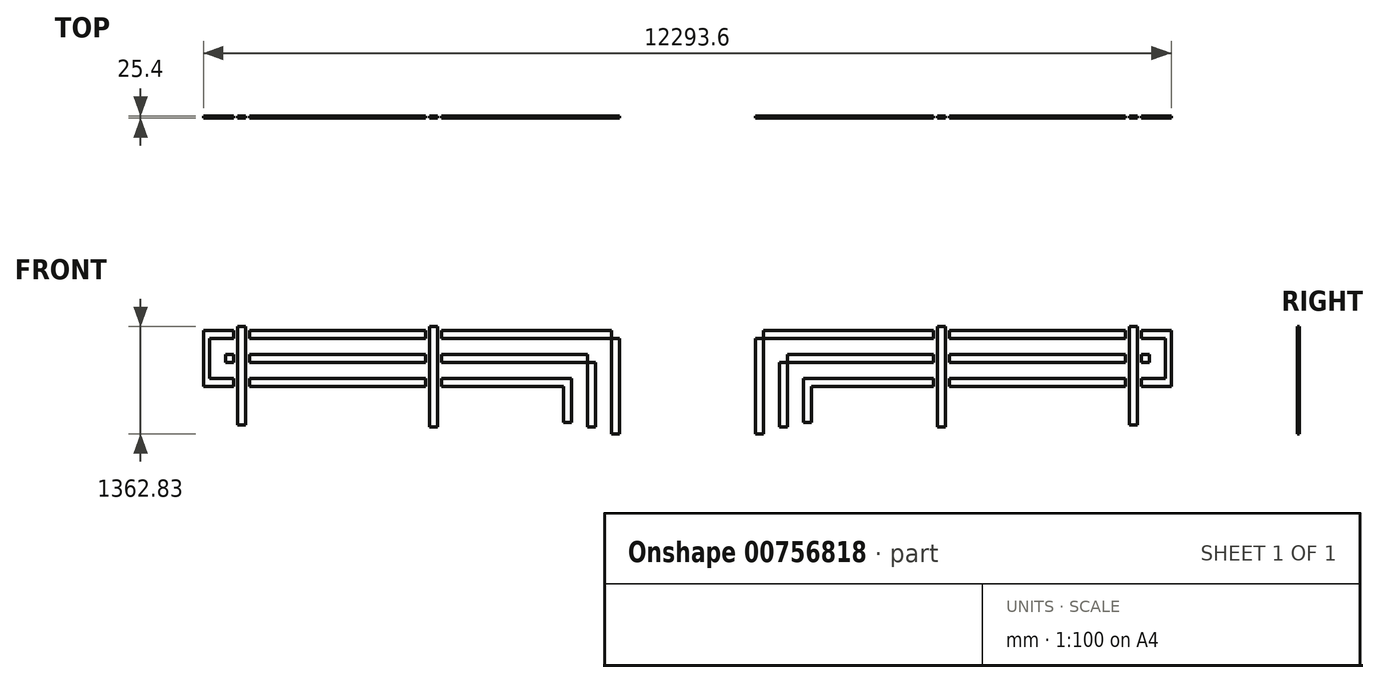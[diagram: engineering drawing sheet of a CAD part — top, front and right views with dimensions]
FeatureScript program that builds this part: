
annotation { "Feature Type Name" : "Feature", "Feature Type Description" : "" }
export const myFeature = defineFeature(function(context is Context, id is Id, definition is map)
    precondition{}
    {
        {
            var Q0;
            Q0=qCreatedBy(makeId("Front.planeOp"),FACE);
            var sketch = newSketch(context, id + "F0", { "sketchPlane" : qUnion([Q0])});
            skLineSegment(sketch, "E0.bottom", {"start": v(-6267.86, -850.3) * mm, "end": v(8083.14, -850.3) * mm});
            skLineSegment(sketch, "E0.top", {"start": v(-6267.86, 673.7) * mm, "end": v(8083.14, 673.7) * mm});
            skLineSegment(sketch, "E0.left", {"start": v(-6267.86, -850.3) * mm, "end": v(-6267.86, 673.7) * mm});
            skLineSegment(sketch, "E0.right", {"start": v(8083.14, -850.3) * mm, "end": v(8083.14, 673.7) * mm});
            skLineSegment(sketch, "E1", {"start": v(-6267.86, -88.3) * mm, "end": v(8083.14, -88.3) * mm});
            skLineSegment(sketch, "E2", {"start": v(82.14, 610.2) * mm, "end": v(56.74, 610.2) * mm});
            skLineSegment(sketch, "E3", {"start": v(82.14, 610.2) * mm, "end": v(82.14, -786.8) * mm});
            skLineSegment(sketch, "E4", {"start": v(82.14, -786.8) * mm, "end": v(56.74, -786.8) * mm});
            skLineSegment(sketch, "E5", {"start": v(56.74, 610.2) * mm, "end": v(-2229.26, 610.2) * mm});
            skLineSegment(sketch, "E6", {"start": v(-2229.26, 610.2) * mm, "end": v(-2229.26, 584.8) * mm});
            skLineSegment(sketch, "E7", {"start": v(-2229.26, 584.8) * mm, "end": v(-2229.26, 457.8) * mm});
            skLineSegment(sketch, "E8", {"start": v(-2229.26, 457.8) * mm, "end": v(-2229.26, 432.4) * mm});
            skLineSegment(sketch, "E9", {"start": v(-2229.26, 432.4) * mm, "end": v(-2229.26, 305.4) * mm});
            skLineSegment(sketch, "E10", {"start": v(-2229.26, 305.4) * mm, "end": v(-2229.26, 280) * mm});
            skLineSegment(sketch, "E11", {"start": v(-2229.26, 280) * mm, "end": v(-2229.26, 153) * mm});
            skLineSegment(sketch, "E12", {"start": v(-2229.26, 153) * mm, "end": v(-2229.26, 127.6) * mm});
            skLineSegment(sketch, "E13", {"start": v(-2229.26, 127.6) * mm, "end": v(-2229.26, 0.6) * mm});
            skLineSegment(sketch, "E14", {"start": v(-2229.26, 0.6) * mm, "end": v(-2229.26, -24.8) * mm});
            skLineSegment(sketch, "E15", {"start": v(-2229.26, -24.8) * mm, "end": v(-2229.26, -151.8) * mm});
            skLineSegment(sketch, "E16", {"start": v(-2229.26, -151.8) * mm, "end": v(-2229.26, -177.2) * mm});
            skLineSegment(sketch, "E17", {"start": v(-2229.26, 584.8) * mm, "end": v(56.74, 584.8) * mm});
            skLineSegment(sketch, "E18", {"start": v(56.74, 610.2) * mm, "end": v(-70.26, 610.2) * mm});
            skLineSegment(sketch, "E19", {"start": v(-70.26, 610.2) * mm, "end": v(-95.66, 610.2) * mm});
            skLineSegment(sketch, "E20", {"start": v(-95.66, 610.2) * mm, "end": v(-222.66, 610.2) * mm});
            skLineSegment(sketch, "E21", {"start": v(-222.66, 610.2) * mm, "end": v(-248.06, 610.2) * mm});
            skLineSegment(sketch, "E22", {"start": v(-248.06, 610.2) * mm, "end": v(-375.06, 610.2) * mm});
            skLineSegment(sketch, "E23", {"start": v(-375.06, 610.2) * mm, "end": v(-400.46, 610.2) * mm});
            skLineSegment(sketch, "E24", {"start": v(-400.46, 610.2) * mm, "end": v(-527.46, 610.2) * mm});
            skLineSegment(sketch, "E25", {"start": v(-527.46, 610.2) * mm, "end": v(-552.86, 610.2) * mm});
            skLineSegment(sketch, "E26", {"start": v(-552.86, 610.2) * mm, "end": v(-679.86, 610.2) * mm});
            skLineSegment(sketch, "E27", {"start": v(-679.86, 610.2) * mm, "end": v(-705.26, 610.2) * mm});
            skLineSegment(sketch, "E28", {"start": v(-2229.26, 457.8) * mm, "end": v(-70.26, 457.8) * mm});
            skLineSegment(sketch, "E29", {"start": v(-2229.26, 432.4) * mm, "end": v(-95.66, 432.4) * mm});
            skLineSegment(sketch, "E30", {"start": v(-2229.26, 153) * mm, "end": v(-375.06, 153) * mm});
            skLineSegment(sketch, "E31", {"start": v(-2229.26, 127.6) * mm, "end": v(-400.46, 127.6) * mm});
            skLineSegment(sketch, "E32", {"start": v(-2229.26, 0.6) * mm, "end": v(-527.46, 0.6) * mm});
            skLineSegment(sketch, "E33", {"start": v(-2229.26, -24.8) * mm, "end": v(-552.86, -24.8) * mm});
            skLineSegment(sketch, "E34", {"start": v(-2229.26, -151.8) * mm, "end": v(-679.86, -151.8) * mm});
            skLineSegment(sketch, "E35", {"start": v(-2229.26, -177.2) * mm, "end": v(-705.26, -177.2) * mm});
            skLineSegment(sketch, "E36", {"start": v(-95.66, 432.4) * mm, "end": v(-95.66, -786.8) * mm});
            skLineSegment(sketch, "E37", {"start": v(-95.66, -786.8) * mm, "end": v(82.14, -786.8) * mm});
            skLineSegment(sketch, "E38", {"start": v(-400.46, -689.48) * mm, "end": v(-400.46, 127.6) * mm});
            skLineSegment(sketch, "E39", {"start": v(-527.46, 0.6) * mm, "end": v(-527.46, -634.4) * mm});
            skLineSegment(sketch, "E40", {"start": v(-527.46, -634.4) * mm, "end": v(-705.26, -634.4) * mm});
            skLineSegment(sketch, "E41", {"start": v(-705.26, -634.4) * mm, "end": v(-705.26, -177.2) * mm});
            skLineSegment(sketch, "E42", {"start": v(-2229.26, 305.4) * mm, "end": v(-222.66, 305.4) * mm});
            skLineSegment(sketch, "E43", {"start": v(-2229.26, 280) * mm, "end": v(-248.06, 280) * mm});
            skLineSegment(sketch, "E44", {"start": v(-222.66, 305.4) * mm, "end": v(-222.66, -689.48) * mm});
            skLineSegment(sketch, "E45", {"start": v(-400.46, -689.48) * mm, "end": v(-222.66, -689.48) * mm});
            skLineSegment(sketch, "E46", {"start": v(-2229.26, 610.2) * mm, "end": v(-2229.26, 661) * mm});
            skLineSegment(sketch, "E47", {"start": v(-2229.26, 661) * mm, "end": v(-2229.26, -689.48) * mm});
            skLineSegment(sketch, "E48", {"start": v(-2229.26, -689.48) * mm, "end": v(-2407.06, -689.48) * mm});
            skLineSegment(sketch, "E49", {"start": v(-2407.06, -689.48) * mm, "end": v(-2407.06, 661) * mm});
            skLineSegment(sketch, "E50", {"start": v(-2407.06, 661) * mm, "end": v(-2229.26, 661) * mm});
            skLineSegment(sketch, "E51.bottom", {"start": v(-2229.26, 661) * mm, "end": v(-2254.66, 661) * mm});
            skLineSegment(sketch, "E51.top", {"start": v(-2229.26, 635.6) * mm, "end": v(-2254.66, 635.6) * mm});
            skLineSegment(sketch, "E51.left", {"start": v(-2229.26, 661) * mm, "end": v(-2229.26, 635.6) * mm});
            skLineSegment(sketch, "E51.right", {"start": v(-2254.66, 661) * mm, "end": v(-2254.66, 635.6) * mm});
            skLineSegment(sketch, "E52.bottom", {"start": v(-2407.06, -689.48) * mm, "end": v(-2381.66, -689.48) * mm});
            skLineSegment(sketch, "E52.top", {"start": v(-2407.06, -664.08) * mm, "end": v(-2381.66, -664.08) * mm});
            skLineSegment(sketch, "E52.left", {"start": v(-2407.06, -689.48) * mm, "end": v(-2407.06, -664.08) * mm});
            skLineSegment(sketch, "E52.right", {"start": v(-2381.66, -689.48) * mm, "end": v(-2381.66, -664.08) * mm});
            skLineSegment(sketch, "E53.bottom", {"start": v(-2254.66, 635.6) * mm, "end": v(-2381.66, 635.6) * mm});
            skLineSegment(sketch, "E53.top", {"start": v(-2254.66, -664.08) * mm, "end": v(-2381.66, -664.08) * mm});
            skLineSegment(sketch, "E53.left", {"start": v(-2254.66, 635.6) * mm, "end": v(-2254.66, -664.08) * mm});
            skLineSegment(sketch, "E53.right", {"start": v(-2381.66, 635.6) * mm, "end": v(-2381.66, -664.08) * mm});
            skLineSegment(sketch, "E54.bottom", {"start": v(-705.26, -634.4) * mm, "end": v(-679.86, -634.4) * mm});
            skLineSegment(sketch, "E54.top", {"start": v(-705.26, -609) * mm, "end": v(-679.86, -609) * mm});
            skLineSegment(sketch, "E54.left", {"start": v(-705.26, -634.4) * mm, "end": v(-705.26, -609) * mm});
            skLineSegment(sketch, "E54.right", {"start": v(-679.86, -634.4) * mm, "end": v(-679.86, -609) * mm});
            skLineSegment(sketch, "E55", {"start": v(-679.86, -151.8) * mm, "end": v(-679.86, -609) * mm});
            skLineSegment(sketch, "E56", {"start": v(-552.86, -609) * mm, "end": v(-679.86, -609) * mm});
            skLineSegment(sketch, "E57", {"start": v(-552.86, -609) * mm, "end": v(-552.86, -24.8) * mm});
            skLineSegment(sketch, "E58.bottom", {"start": v(-222.66, -689.48) * mm, "end": v(-248.06, -689.48) * mm});
            skLineSegment(sketch, "E58.top", {"start": v(-222.66, -664.08) * mm, "end": v(-248.06, -664.08) * mm});
            skLineSegment(sketch, "E58.left", {"start": v(-222.66, -689.48) * mm, "end": v(-222.66, -664.08) * mm});
            skLineSegment(sketch, "E58.right", {"start": v(-248.06, -689.48) * mm, "end": v(-248.06, -664.08) * mm});
            skLineSegment(sketch, "E59.bottom", {"start": v(-95.66, -786.8) * mm, "end": v(-70.26, -786.8) * mm});
            skLineSegment(sketch, "E59.top", {"start": v(-95.66, -752.63) * mm, "end": v(-70.26, -752.63) * mm});
            skLineSegment(sketch, "E59.left", {"start": v(-95.66, -786.8) * mm, "end": v(-95.66, -752.63) * mm});
            skLineSegment(sketch, "E59.right", {"start": v(-70.26, -786.8) * mm, "end": v(-70.26, -752.63) * mm});
            skLineSegment(sketch, "E60", {"start": v(-248.06, 280) * mm, "end": v(-248.06, -664.08) * mm});
            skLineSegment(sketch, "E61", {"start": v(-375.06, 153) * mm, "end": v(-375.06, -664.08) * mm});
            skLineSegment(sketch, "E62", {"start": v(-375.06, -664.08) * mm, "end": v(-248.06, -664.08) * mm});
            skLineSegment(sketch, "E63", {"start": v(-70.26, 457.8) * mm, "end": v(-70.26, -752.63) * mm});
            skLineSegment(sketch, "E64", {"start": v(56.74, -752.63) * mm, "end": v(-70.26, -752.63) * mm});
            skLineSegment(sketch, "E65", {"start": v(56.74, -752.63) * mm, "end": v(56.74, 584.8) * mm});
            skLineSegment(sketch, "E66.MirrorCS", {"start": v(1733.14, 610.2) * mm, "end": v(1733.14, -786.8) * mm});
            skLineSegment(sketch, "E67.MirrorCS", {"start": v(1758.54, -752.63) * mm, "end": v(1758.54, 584.8) * mm});
            skLineSegment(sketch, "E68.MirrorCS", {"start": v(1885.54, 457.8) * mm, "end": v(1885.54, -752.63) * mm});
            skLineSegment(sketch, "E69.MirrorCS", {"start": v(1910.94, 432.4) * mm, "end": v(1910.94, -786.8) * mm});
            skLineSegment(sketch, "E70.MirrorCS", {"start": v(2037.94, 305.4) * mm, "end": v(2037.94, -689.48) * mm});
            skLineSegment(sketch, "E71.MirrorCS", {"start": v(2063.34, 280) * mm, "end": v(2063.34, -664.08) * mm});
            skLineSegment(sketch, "E72.MirrorCS", {"start": v(2190.34, 153) * mm, "end": v(2190.34, -664.08) * mm});
            skLineSegment(sketch, "E73.MirrorCS", {"start": v(2215.74, -689.48) * mm, "end": v(2215.74, 127.6) * mm});
            skLineSegment(sketch, "E74.MirrorCS", {"start": v(2342.74, 0.6) * mm, "end": v(2342.74, -634.4) * mm});
            skLineSegment(sketch, "E75.MirrorCS", {"start": v(2368.14, -609) * mm, "end": v(2368.14, -24.8) * mm});
            skLineSegment(sketch, "E76.MirrorCS", {"start": v(2495.14, -151.8) * mm, "end": v(2495.14, -609) * mm});
            skLineSegment(sketch, "E77.MirrorCS", {"start": v(2520.54, -634.4) * mm, "end": v(2520.54, -177.2) * mm});
            skLineSegment(sketch, "E78.MirrorCS", {"start": v(1910.94, -786.8) * mm, "end": v(1733.14, -786.8) * mm});
            skLineSegment(sketch, "E79.MirrorCS", {"start": v(1758.54, -752.63) * mm, "end": v(1885.54, -752.63) * mm});
            skLineSegment(sketch, "E80.MirrorCS", {"start": v(2215.74, -689.48) * mm, "end": v(2037.94, -689.48) * mm});
            skLineSegment(sketch, "E81.MirrorCS", {"start": v(2190.34, -664.08) * mm, "end": v(2063.34, -664.08) * mm});
            skLineSegment(sketch, "E82.MirrorCS", {"start": v(2342.74, -634.4) * mm, "end": v(2520.54, -634.4) * mm});
            skLineSegment(sketch, "E83.MirrorCS", {"start": v(2368.14, -609) * mm, "end": v(2495.14, -609) * mm});
            skLineSegment(sketch, "E84.MirrorCS", {"start": v(4044.54, -177.2) * mm, "end": v(2520.54, -177.2) * mm});
            skLineSegment(sketch, "E85.MirrorCS", {"start": v(4044.54, -151.8) * mm, "end": v(2495.14, -151.8) * mm});
            skLineSegment(sketch, "E86.MirrorCS", {"start": v(4044.54, -24.8) * mm, "end": v(2368.14, -24.8) * mm});
            skLineSegment(sketch, "E87.MirrorCS", {"start": v(4044.54, 0.6) * mm, "end": v(2342.74, 0.6) * mm});
            skLineSegment(sketch, "E88.MirrorCS", {"start": v(4044.54, 127.6) * mm, "end": v(2215.74, 127.6) * mm});
            skLineSegment(sketch, "E89.MirrorCS", {"start": v(4044.54, 153) * mm, "end": v(2190.34, 153) * mm});
            skLineSegment(sketch, "E90.MirrorCS", {"start": v(4044.54, 280) * mm, "end": v(2063.34, 280) * mm});
            skLineSegment(sketch, "E91.MirrorCS", {"start": v(4044.54, 305.4) * mm, "end": v(2037.94, 305.4) * mm});
            skLineSegment(sketch, "E92.MirrorCS", {"start": v(4044.54, 432.4) * mm, "end": v(1910.94, 432.4) * mm});
            skLineSegment(sketch, "E93.MirrorCS", {"start": v(4044.54, 457.8) * mm, "end": v(1885.54, 457.8) * mm});
            skLineSegment(sketch, "E94.MirrorCS", {"start": v(4044.54, 584.8) * mm, "end": v(1758.54, 584.8) * mm});
            skLineSegment(sketch, "E95.MirrorCS", {"start": v(1758.54, 610.2) * mm, "end": v(4044.54, 610.2) * mm});
            skLineSegment(sketch, "E96.MirrorCS", {"start": v(4044.54, 661) * mm, "end": v(4044.54, -689.48) * mm});
            skLineSegment(sketch, "E97.MirrorCS", {"start": v(4069.94, 635.6) * mm, "end": v(4069.94, -664.08) * mm});
            skLineSegment(sketch, "E98.MirrorCS", {"start": v(4196.94, 635.6) * mm, "end": v(4196.94, -664.08) * mm});
            skLineSegment(sketch, "E99.MirrorCS", {"start": v(4222.34, -689.48) * mm, "end": v(4222.34, 661) * mm});
            skLineSegment(sketch, "E100.MirrorCS", {"start": v(4069.94, -664.08) * mm, "end": v(4196.94, -664.08) * mm});
            skLineSegment(sketch, "E101.MirrorCS", {"start": v(4044.54, -689.48) * mm, "end": v(4222.34, -689.48) * mm});
            skLineSegment(sketch, "E102.MirrorCS", {"start": v(4069.94, 635.6) * mm, "end": v(4196.94, 635.6) * mm});
            skLineSegment(sketch, "E103.MirrorCS", {"start": v(4222.34, 661) * mm, "end": v(4044.54, 661) * mm});
            skLineSegment(sketch, "E104", {"start": v(1733.14, 610.2) * mm, "end": v(1758.54, 610.2) * mm});
            skLineSegment(sketch, "E105", {"start": v(-2407.06, 661) * mm, "end": v(-2407.06, 610.2) * mm});
            skLineSegment(sketch, "E106", {"start": v(-2407.06, 610.2) * mm, "end": v(-4693.06, 610.2) * mm});
            skLineSegment(sketch, "E107", {"start": v(-4693.06, 610.2) * mm, "end": v(-4693.06, 432.4) * mm});
            skLineSegment(sketch, "E108", {"start": v(-4693.06, 432.4) * mm, "end": v(-2407.06, 432.4) * mm});
            skLineSegment(sketch, "E109", {"start": v(-2407.06, 432.4) * mm, "end": v(-2407.06, 457.8) * mm});
            skLineSegment(sketch, "E110", {"start": v(-2407.06, 432.4) * mm, "end": v(-2407.06, 305.4) * mm});
            skLineSegment(sketch, "E111", {"start": v(-2407.06, 305.4) * mm, "end": v(-4693.06, 305.4) * mm});
            skLineSegment(sketch, "E112", {"start": v(-4693.06, 305.4) * mm, "end": v(-4693.06, 127.6) * mm});
            skLineSegment(sketch, "E113", {"start": v(-4693.06, 127.6) * mm, "end": v(-2407.06, 127.6) * mm});
            skLineSegment(sketch, "E114", {"start": v(-2407.06, 127.6) * mm, "end": v(-2407.06, 0.6) * mm});
            skLineSegment(sketch, "E115", {"start": v(-2407.06, 0.6) * mm, "end": v(-4693.06, 0.6) * mm});
            skLineSegment(sketch, "E116", {"start": v(-4693.06, 0.6) * mm, "end": v(-4693.06, -177.2) * mm});
            skLineSegment(sketch, "E117", {"start": v(-4693.06, -177.2) * mm, "end": v(-2407.06, -177.2) * mm});
            skLineSegment(sketch, "E118.bottom", {"start": v(-4693.06, -177.2) * mm, "end": v(-4667.66, -177.2) * mm});
            skLineSegment(sketch, "E118.top", {"start": v(-4693.06, -151.8) * mm, "end": v(-4667.66, -151.8) * mm});
            skLineSegment(sketch, "E118.left", {"start": v(-4693.06, -177.2) * mm, "end": v(-4693.06, -151.8) * mm});
            skLineSegment(sketch, "E118.right", {"start": v(-4667.66, -177.2) * mm, "end": v(-4667.66, -151.8) * mm});
            skLineSegment(sketch, "E119.bottom", {"start": v(-4693.06, 127.6) * mm, "end": v(-4667.66, 127.6) * mm});
            skLineSegment(sketch, "E119.top", {"start": v(-4693.06, 153) * mm, "end": v(-4667.66, 153) * mm});
            skLineSegment(sketch, "E119.left", {"start": v(-4693.06, 127.6) * mm, "end": v(-4693.06, 153) * mm});
            skLineSegment(sketch, "E119.right", {"start": v(-4667.66, 127.6) * mm, "end": v(-4667.66, 153) * mm});
            skLineSegment(sketch, "E120.bottom", {"start": v(-4693.06, 432.4) * mm, "end": v(-4667.66, 432.4) * mm});
            skLineSegment(sketch, "E120.top", {"start": v(-4693.06, 457.8) * mm, "end": v(-4667.66, 457.8) * mm});
            skLineSegment(sketch, "E120.left", {"start": v(-4693.06, 432.4) * mm, "end": v(-4693.06, 457.8) * mm});
            skLineSegment(sketch, "E120.right", {"start": v(-4667.66, 432.4) * mm, "end": v(-4667.66, 457.8) * mm});
            skLineSegment(sketch, "E121", {"start": v(-2407.06, 457.8) * mm, "end": v(-4667.66, 457.8) * mm});
            skLineSegment(sketch, "E122", {"start": v(-4667.66, 584.8) * mm, "end": v(-4667.66, 457.8) * mm});
            skLineSegment(sketch, "E123", {"start": v(-4667.66, 584.8) * mm, "end": v(-2407.06, 584.8) * mm});
            skLineSegment(sketch, "E124", {"start": v(-4667.66, 153) * mm, "end": v(-2407.06, 153) * mm});
            skLineSegment(sketch, "E125", {"start": v(-4667.66, 153) * mm, "end": v(-4667.66, 280) * mm});
            skLineSegment(sketch, "E126", {"start": v(-4667.66, 280) * mm, "end": v(-2407.06, 280) * mm});
            skLineSegment(sketch, "E127", {"start": v(-4667.66, -151.8) * mm, "end": v(-4667.66, -24.8) * mm});
            skLineSegment(sketch, "E128", {"start": v(-4667.66, -24.8) * mm, "end": v(-2407.06, -24.8) * mm});
            skLineSegment(sketch, "E129", {"start": v(-4667.66, -151.8) * mm, "end": v(-2407.06, -151.8) * mm});
            skLineSegment(sketch, "E130", {"start": v(-4693.06, 610.2) * mm, "end": v(-4693.06, 661) * mm});
            skLineSegment(sketch, "E131", {"start": v(-4693.06, 661) * mm, "end": v(-4693.06, -664.08) * mm});
            skLineSegment(sketch, "E132", {"start": v(-4693.06, -664.08) * mm, "end": v(-4667.66, -664.08) * mm});
            skLineSegment(sketch, "E133", {"start": v(-4667.66, -664.08) * mm, "end": v(-4667.66, 661) * mm});
            skLineSegment(sketch, "E134", {"start": v(-4667.66, 661) * mm, "end": v(-4693.06, 661) * mm});
            skLineSegment(sketch, "E135", {"start": v(-4667.66, 661) * mm, "end": v(-4845.46, 661) * mm});
            skLineSegment(sketch, "E136", {"start": v(-4845.46, 661) * mm, "end": v(-4845.46, -664.08) * mm});
            skLineSegment(sketch, "E137", {"start": v(-4845.46, -664.08) * mm, "end": v(-4693.06, -664.08) * mm});
            skLineSegment(sketch, "E138.bottom", {"start": v(-4667.66, -664.08) * mm, "end": v(-4693.06, -664.08) * mm});
            skLineSegment(sketch, "E138.top", {"start": v(-4667.66, -638.68) * mm, "end": v(-4693.06, -638.68) * mm});
            skLineSegment(sketch, "E138.left", {"start": v(-4667.66, -664.08) * mm, "end": v(-4667.66, -638.68) * mm});
            skLineSegment(sketch, "E138.right", {"start": v(-4693.06, -664.08) * mm, "end": v(-4693.06, -638.68) * mm});
            skLineSegment(sketch, "E139.bottom", {"start": v(-4845.46, -664.08) * mm, "end": v(-4820.06, -664.08) * mm});
            skLineSegment(sketch, "E139.top", {"start": v(-4845.46, -638.68) * mm, "end": v(-4820.06, -638.68) * mm});
            skLineSegment(sketch, "E139.left", {"start": v(-4845.46, -664.08) * mm, "end": v(-4845.46, -638.68) * mm});
            skLineSegment(sketch, "E139.right", {"start": v(-4820.06, -664.08) * mm, "end": v(-4820.06, -638.68) * mm});
            skLineSegment(sketch, "E140", {"start": v(-4820.06, -638.68) * mm, "end": v(-4693.06, -638.68) * mm});
            skLineSegment(sketch, "E141.bottom", {"start": v(-4845.46, 661) * mm, "end": v(-4820.06, 661) * mm});
            skLineSegment(sketch, "E141.top", {"start": v(-4845.46, 635.6) * mm, "end": v(-4820.06, 635.6) * mm});
            skLineSegment(sketch, "E141.left", {"start": v(-4845.46, 661) * mm, "end": v(-4845.46, 635.6) * mm});
            skLineSegment(sketch, "E141.right", {"start": v(-4820.06, 661) * mm, "end": v(-4820.06, 635.6) * mm});
            skLineSegment(sketch, "E142", {"start": v(-4820.06, 635.6) * mm, "end": v(-4693.06, 635.6) * mm});
            skLineSegment(sketch, "E143", {"start": v(-4693.06, 635.6) * mm, "end": v(-4820.06, 635.6) * mm});
            skLineSegment(sketch, "E144", {"start": v(-4820.06, 635.6) * mm, "end": v(-4820.06, -638.68) * mm});
            skLineSegment(sketch, "E145", {"start": v(-4845.46, 280) * mm, "end": v(-4972.46, 280) * mm});
            skLineSegment(sketch, "E146", {"start": v(-4972.46, 280) * mm, "end": v(-4972.46, 153) * mm});
            skLineSegment(sketch, "E147", {"start": v(-4972.46, 153) * mm, "end": v(-4845.46, 153) * mm});
            skLineSegment(sketch, "E148", {"start": v(-4845.46, 153) * mm, "end": v(-4845.46, 127.6) * mm});
            skLineSegment(sketch, "E149", {"start": v(-4845.46, 127.6) * mm, "end": v(-4997.86, 127.6) * mm});
            skLineSegment(sketch, "E150", {"start": v(-4997.86, 127.6) * mm, "end": v(-4997.86, 305.4) * mm});
            skLineSegment(sketch, "E151", {"start": v(-4997.86, 305.4) * mm, "end": v(-4845.46, 305.4) * mm});
            skLineSegment(sketch, "E152", {"start": v(-4845.46, 432.4) * mm, "end": v(-5124.86, 432.4) * mm});
            skLineSegment(sketch, "E153", {"start": v(-5124.86, 432.4) * mm, "end": v(-5124.86, 0.6) * mm});
            skLineSegment(sketch, "E154", {"start": v(-5124.86, 0.6) * mm, "end": v(-4845.46, 0.6) * mm});
            skLineSegment(sketch, "E155.bottom", {"start": v(-5124.86, 0.6) * mm, "end": v(-5150.26, 0.6) * mm});
            skLineSegment(sketch, "E155.top", {"start": v(-5124.86, -24.8) * mm, "end": v(-5150.26, -24.8) * mm});
            skLineSegment(sketch, "E155.left", {"start": v(-5124.86, 0.6) * mm, "end": v(-5124.86, -24.8) * mm});
            skLineSegment(sketch, "E155.right", {"start": v(-5150.26, 0.6) * mm, "end": v(-5150.26, -24.8) * mm});
            skLineSegment(sketch, "E156", {"start": v(-5124.86, -24.8) * mm, "end": v(-4845.46, -24.8) * mm});
            skLineSegment(sketch, "E157", {"start": v(-5150.26, 0.6) * mm, "end": v(-5150.26, 457.8) * mm});
            skLineSegment(sketch, "E158", {"start": v(-5150.26, 457.8) * mm, "end": v(-4845.46, 457.8) * mm});
            skLineSegment(sketch, "E159", {"start": v(-4845.46, 661) * mm, "end": v(-4845.46, 610.2) * mm});
            skLineSegment(sketch, "E160", {"start": v(-5277.26, -177.2) * mm, "end": v(-4845.46, -177.2) * mm});
            skLineSegment(sketch, "E161.bottom", {"start": v(-5277.26, -177.2) * mm, "end": v(-5251.86, -177.2) * mm});
            skLineSegment(sketch, "E161.top", {"start": v(-5277.26, -151.8) * mm, "end": v(-5251.86, -151.8) * mm});
            skLineSegment(sketch, "E161.left", {"start": v(-5277.26, -177.2) * mm, "end": v(-5277.26, -151.8) * mm});
            skLineSegment(sketch, "E161.right", {"start": v(-5251.86, -177.2) * mm, "end": v(-5251.86, -151.8) * mm});
            skLineSegment(sketch, "E162", {"start": v(-5251.86, -151.8) * mm, "end": v(-4845.46, -151.8) * mm});
            skLineSegment(sketch, "E163", {"start": v(-5251.86, -151.8) * mm, "end": v(-5251.86, 584.8) * mm});
            skLineSegment(sketch, "E164.MirrorCS", {"start": v(6508.34, -177.2) * mm, "end": v(4222.34, -177.2) * mm});
            skLineSegment(sketch, "E165.MirrorCS", {"start": v(6482.94, -151.8) * mm, "end": v(4222.34, -151.8) * mm});
            skLineSegment(sketch, "E166.MirrorCS", {"start": v(6482.94, -24.8) * mm, "end": v(4222.34, -24.8) * mm});
            skLineSegment(sketch, "E167.MirrorCS", {"start": v(4222.34, 0.6) * mm, "end": v(6508.34, 0.6) * mm});
            skLineSegment(sketch, "E168.MirrorCS", {"start": v(6508.34, 127.6) * mm, "end": v(4222.34, 127.6) * mm});
            skLineSegment(sketch, "E169.MirrorCS", {"start": v(6482.94, 153) * mm, "end": v(4222.34, 153) * mm});
            skLineSegment(sketch, "E170.MirrorCS", {"start": v(6482.94, 280) * mm, "end": v(4222.34, 280) * mm});
            skLineSegment(sketch, "E171.MirrorCS", {"start": v(4222.34, 305.4) * mm, "end": v(6508.34, 305.4) * mm});
            skLineSegment(sketch, "E172.MirrorCS", {"start": v(6508.34, 432.4) * mm, "end": v(4222.34, 432.4) * mm});
            skLineSegment(sketch, "E173.MirrorCS", {"start": v(4222.34, 457.8) * mm, "end": v(6482.94, 457.8) * mm});
            skLineSegment(sketch, "E174.MirrorCS", {"start": v(6482.94, 584.8) * mm, "end": v(4222.34, 584.8) * mm});
            skLineSegment(sketch, "E175.MirrorCS", {"start": v(4222.34, 610.2) * mm, "end": v(6508.34, 610.2) * mm});
            skLineSegment(sketch, "E176.MirrorCS", {"start": v(6482.94, -664.08) * mm, "end": v(6482.94, 661) * mm});
            skLineSegment(sketch, "E177.MirrorCS", {"start": v(6508.34, 661) * mm, "end": v(6508.34, -664.08) * mm});
            skLineSegment(sketch, "E178.MirrorCS", {"start": v(6635.34, -638.68) * mm, "end": v(6508.34, -638.68) * mm});
            skLineSegment(sketch, "E179.MirrorCS", {"start": v(6660.74, -664.08) * mm, "end": v(6508.34, -664.08) * mm});
            skLineSegment(sketch, "E180.MirrorCS", {"start": v(6635.34, 635.6) * mm, "end": v(6635.34, -638.68) * mm});
            skLineSegment(sketch, "E181.MirrorCS", {"start": v(6660.74, 661) * mm, "end": v(6660.74, -664.08) * mm});
            skLineSegment(sketch, "E182.MirrorCS", {"start": v(6482.94, 661) * mm, "end": v(6660.74, 661) * mm});
            skLineSegment(sketch, "E183.MirrorCS", {"start": v(6508.34, 635.6) * mm, "end": v(6635.34, 635.6) * mm});
            skLineSegment(sketch, "E184.MirrorCS", {"start": v(7067.14, 584.8) * mm, "end": v(6660.74, 584.8) * mm});
            skLineSegment(sketch, "E185.MirrorCS", {"start": v(6660.74, 610.2) * mm, "end": v(7092.54, 610.2) * mm});
            skLineSegment(sketch, "E186.MirrorCS", {"start": v(6965.54, 457.8) * mm, "end": v(6660.74, 457.8) * mm});
            skLineSegment(sketch, "E187.MirrorCS", {"start": v(6660.74, 432.4) * mm, "end": v(6940.14, 432.4) * mm});
            skLineSegment(sketch, "E188.MirrorCS", {"start": v(6813.14, 305.4) * mm, "end": v(6660.74, 305.4) * mm});
            skLineSegment(sketch, "E189.MirrorCS", {"start": v(6787.74, 153) * mm, "end": v(6660.74, 153) * mm});
            skLineSegment(sketch, "E190.MirrorCS", {"start": v(6660.74, 127.6) * mm, "end": v(6813.14, 127.6) * mm});
            skLineSegment(sketch, "E191.MirrorCS", {"start": v(6940.14, 0.6) * mm, "end": v(6660.74, 0.6) * mm});
            skLineSegment(sketch, "E192.MirrorCS", {"start": v(6940.14, -24.8) * mm, "end": v(6660.74, -24.8) * mm});
            skLineSegment(sketch, "E193.MirrorCS", {"start": v(7067.14, -151.8) * mm, "end": v(6660.74, -151.8) * mm});
            skLineSegment(sketch, "E194.MirrorCS", {"start": v(7092.54, -177.2) * mm, "end": v(6660.74, -177.2) * mm});
            skLineSegment(sketch, "E195.MirrorCS", {"start": v(7092.54, 610.2) * mm, "end": v(7092.54, -177.2) * mm});
            skLineSegment(sketch, "E196.MirrorCS", {"start": v(7067.14, -151.8) * mm, "end": v(7067.14, 584.8) * mm});
            skLineSegment(sketch, "E197.MirrorCS", {"start": v(6965.54, 0.6) * mm, "end": v(6965.54, 457.8) * mm});
            skLineSegment(sketch, "E198.MirrorCS", {"start": v(6940.14, 432.4) * mm, "end": v(6940.14, 0.6) * mm});
            skLineSegment(sketch, "E199.MirrorCS", {"start": v(6813.14, 127.6) * mm, "end": v(6813.14, 305.4) * mm});
            skLineSegment(sketch, "E200.MirrorCS", {"start": v(6787.74, 280) * mm, "end": v(6787.74, 153) * mm});
            skLineSegment(sketch, "E201", {"start": v(6787.74, 280) * mm, "end": v(6660.74, 280) * mm});
            skLineSegment(sketch, "E202.bottom", {"start": v(6965.54, 0.6) * mm, "end": v(6940.14, 0.6) * mm});
            skLineSegment(sketch, "E202.top", {"start": v(6965.54, -24.8) * mm, "end": v(6940.14, -24.8) * mm});
            skLineSegment(sketch, "E202.left", {"start": v(6965.54, 0.6) * mm, "end": v(6965.54, -24.8) * mm});
            skLineSegment(sketch, "E202.right", {"start": v(6940.14, 0.6) * mm, "end": v(6940.14, -24.8) * mm});
            skLineSegment(sketch, "E203", {"start": v(6482.94, -664.08) * mm, "end": v(6508.34, -664.08) * mm});
            skLineSegment(sketch, "E204.bottom", {"start": v(-5251.86, -151.8) * mm, "end": v(-5239.16, -151.8) * mm});
            skLineSegment(sketch, "E204.top", {"start": v(-5251.86, -139.1) * mm, "end": v(-5239.16, -139.1) * mm});
            skLineSegment(sketch, "E204.left", {"start": v(-5251.86, -151.8) * mm, "end": v(-5251.86, -139.1) * mm});
            skLineSegment(sketch, "E204.right", {"start": v(-5239.16, -151.8) * mm, "end": v(-5239.16, -139.1) * mm});
            skLineSegment(sketch, "E205.bottom", {"start": v(-5124.86, 0.6) * mm, "end": v(-5112.16, 0.6) * mm});
            skLineSegment(sketch, "E205.top", {"start": v(-5124.86, 13.3) * mm, "end": v(-5112.16, 13.3) * mm});
            skLineSegment(sketch, "E205.left", {"start": v(-5124.86, 0.6) * mm, "end": v(-5124.86, 13.3) * mm});
            skLineSegment(sketch, "E205.right", {"start": v(-5112.16, 0.6) * mm, "end": v(-5112.16, 13.3) * mm});
            skLineSegment(sketch, "E206.bottom", {"start": v(-4972.46, 153) * mm, "end": v(-4959.76, 153) * mm});
            skLineSegment(sketch, "E206.top", {"start": v(-4972.46, 165.7) * mm, "end": v(-4959.76, 165.7) * mm});
            skLineSegment(sketch, "E206.left", {"start": v(-4972.46, 153) * mm, "end": v(-4972.46, 165.7) * mm});
            skLineSegment(sketch, "E206.right", {"start": v(-4959.76, 153) * mm, "end": v(-4959.76, 165.7) * mm});
            skLineSegment(sketch, "E207.bottom", {"start": v(-4845.46, 0.6) * mm, "end": v(-4858.16, 0.6) * mm});
            skLineSegment(sketch, "E207.top", {"start": v(-4845.46, 13.3) * mm, "end": v(-4858.16, 13.3) * mm});
            skLineSegment(sketch, "E207.left", {"start": v(-4845.46, 0.6) * mm, "end": v(-4845.46, 13.3) * mm});
            skLineSegment(sketch, "E207.right", {"start": v(-4858.16, 0.6) * mm, "end": v(-4858.16, 13.3) * mm});
            skLineSegment(sketch, "E208.bottom", {"start": v(-4845.46, -151.8) * mm, "end": v(-4858.16, -151.8) * mm});
            skLineSegment(sketch, "E208.top", {"start": v(-4845.46, -139.1) * mm, "end": v(-4858.16, -139.1) * mm});
            skLineSegment(sketch, "E208.left", {"start": v(-4845.46, -151.8) * mm, "end": v(-4845.46, -139.1) * mm});
            skLineSegment(sketch, "E208.right", {"start": v(-4858.16, -151.8) * mm, "end": v(-4858.16, -139.1) * mm});
            skLineSegment(sketch, "E209.bottom", {"start": v(-4845.46, -24.8) * mm, "end": v(-4858.16, -24.8) * mm});
            skLineSegment(sketch, "E209.top", {"start": v(-4845.46, -37.5) * mm, "end": v(-4858.16, -37.5) * mm});
            skLineSegment(sketch, "E209.left", {"start": v(-4845.46, -24.8) * mm, "end": v(-4845.46, -37.5) * mm});
            skLineSegment(sketch, "E209.right", {"start": v(-4858.16, -24.8) * mm, "end": v(-4858.16, -37.5) * mm});
            skLineSegment(sketch, "E210.bottom", {"start": v(-4845.46, 584.8) * mm, "end": v(-4858.16, 584.8) * mm});
            skLineSegment(sketch, "E210.top", {"start": v(-4845.46, 572.1) * mm, "end": v(-4858.16, 572.1) * mm});
            skLineSegment(sketch, "E210.left", {"start": v(-4845.46, 584.8) * mm, "end": v(-4845.46, 572.1) * mm});
            skLineSegment(sketch, "E210.right", {"start": v(-4858.16, 584.8) * mm, "end": v(-4858.16, 572.1) * mm});
            skLineSegment(sketch, "E211.bottom", {"start": v(-4845.46, 432.4) * mm, "end": v(-4858.16, 432.4) * mm});
            skLineSegment(sketch, "E211.top", {"start": v(-4845.46, 419.7) * mm, "end": v(-4858.16, 419.7) * mm});
            skLineSegment(sketch, "E211.left", {"start": v(-4845.46, 432.4) * mm, "end": v(-4845.46, 419.7) * mm});
            skLineSegment(sketch, "E211.right", {"start": v(-4858.16, 432.4) * mm, "end": v(-4858.16, 419.7) * mm});
            skLineSegment(sketch, "E212.bottom", {"start": v(-4997.86, 305.4) * mm, "end": v(-5010.56, 305.4) * mm});
            skLineSegment(sketch, "E212.top", {"start": v(-4997.86, 318.1) * mm, "end": v(-5010.56, 318.1) * mm});
            skLineSegment(sketch, "E212.left", {"start": v(-4997.86, 305.4) * mm, "end": v(-4997.86, 318.1) * mm});
            skLineSegment(sketch, "E212.right", {"start": v(-5010.56, 305.4) * mm, "end": v(-5010.56, 318.1) * mm});
            skLineSegment(sketch, "E213.top", {"start": v(-5004.2, 114.9) * mm, "end": v(-5016.9, 114.9) * mm});
            skLineSegment(sketch, "E214.bottom", {"start": v(-5150.26, 457.8) * mm, "end": v(-5162.96, 457.8) * mm});
            skLineSegment(sketch, "E214.top", {"start": v(-5150.26, 470.5) * mm, "end": v(-5162.96, 470.5) * mm});
            skLineSegment(sketch, "E214.left", {"start": v(-5150.26, 457.8) * mm, "end": v(-5150.26, 470.5) * mm});
            skLineSegment(sketch, "E214.right", {"start": v(-5162.96, 457.8) * mm, "end": v(-5162.96, 470.5) * mm});
            skLineSegment(sketch, "E215.bottom", {"start": v(-5251.86, 584.8) * mm, "end": v(-5239.16, 584.8) * mm});
            skLineSegment(sketch, "E215.top", {"start": v(-5251.86, 572.1) * mm, "end": v(-5239.16, 572.1) * mm});
            skLineSegment(sketch, "E215.left", {"start": v(-5251.86, 584.8) * mm, "end": v(-5251.86, 572.1) * mm});
            skLineSegment(sketch, "E215.right", {"start": v(-5239.16, 584.8) * mm, "end": v(-5239.16, 572.1) * mm});
            skLineSegment(sketch, "E216", {"start": v(-4858.16, -139.1) * mm, "end": v(-5239.16, -139.1) * mm});
            skLineSegment(sketch, "E217", {"start": v(-5239.16, 572.1) * mm, "end": v(-4858.16, 572.1) * mm});
            skLineSegment(sketch, "E218", {"start": v(-5150.26, 470.5) * mm, "end": v(-4858.16, 470.5) * mm});
            skLineSegment(sketch, "E219", {"start": v(-4858.16, 470.5) * mm, "end": v(-4858.16, 572.1) * mm});
            skLineSegment(sketch, "E220", {"start": v(-5239.16, 572.1) * mm, "end": v(-5239.16, -139.1) * mm});
            skLineSegment(sketch, "E221", {"start": v(-5162.96, 457.8) * mm, "end": v(-5162.96, -37.5) * mm});
            skLineSegment(sketch, "E222", {"start": v(-5162.96, -37.5) * mm, "end": v(-4858.16, -37.5) * mm});
            skLineSegment(sketch, "E223", {"start": v(-4858.16, -139.1) * mm, "end": v(-4858.16, -37.5) * mm});
            skLineSegment(sketch, "E224", {"start": v(-5112.16, 13.3) * mm, "end": v(-4858.16, 13.3) * mm});
            skLineSegment(sketch, "E225", {"start": v(-4858.16, 13.3) * mm, "end": v(-4858.16, 114.9) * mm});
            skLineSegment(sketch, "E226.bottom", {"start": v(-4959.76, 165.7) * mm, "end": v(-4858.16, 165.7) * mm});
            skLineSegment(sketch, "E226.top", {"start": v(-4959.76, 267.3) * mm, "end": v(-4858.16, 267.3) * mm});
            skLineSegment(sketch, "E226.left", {"start": v(-4959.76, 165.7) * mm, "end": v(-4959.76, 267.3) * mm});
            skLineSegment(sketch, "E226.right", {"start": v(-4858.16, 165.7) * mm, "end": v(-4858.16, 267.3) * mm});
            skLineSegment(sketch, "E227.bottom", {"start": v(-4997.86, 127.6) * mm, "end": v(-5010.56, 127.6) * mm});
            skLineSegment(sketch, "E227.top", {"start": v(-4997.86, 114.9) * mm, "end": v(-5010.56, 114.9) * mm});
            skLineSegment(sketch, "E227.left", {"start": v(-4997.86, 127.6) * mm, "end": v(-4997.86, 114.9) * mm});
            skLineSegment(sketch, "E227.right", {"start": v(-5010.56, 127.6) * mm, "end": v(-5010.56, 114.9) * mm});
            skLineSegment(sketch, "E228", {"start": v(-4997.86, 114.9) * mm, "end": v(-4858.16, 114.9) * mm});
            skLineSegment(sketch, "E229", {"start": v(-5010.56, 127.6) * mm, "end": v(-5010.56, 318.1) * mm});
            skLineSegment(sketch, "E230", {"start": v(-4858.16, 419.7) * mm, "end": v(-4858.16, 318.1) * mm});
            skLineSegment(sketch, "E231", {"start": v(-4858.16, 318.1) * mm, "end": v(-4997.86, 318.1) * mm});
            skLineSegment(sketch, "E232", {"start": v(-4858.16, 419.7) * mm, "end": v(-5112.16, 419.7) * mm});
            skLineSegment(sketch, "E233", {"start": v(-5112.16, 419.7) * mm, "end": v(-5112.16, 13.3) * mm});
            skLineSegment(sketch, "E234.bottom", {"start": v(-4667.66, -151.8) * mm, "end": v(-4654.96, -151.8) * mm});
            skLineSegment(sketch, "E234.top", {"start": v(-4667.66, -139.1) * mm, "end": v(-4654.96, -139.1) * mm});
            skLineSegment(sketch, "E234.left", {"start": v(-4667.66, -151.8) * mm, "end": v(-4667.66, -139.1) * mm});
            skLineSegment(sketch, "E234.right", {"start": v(-4654.96, -151.8) * mm, "end": v(-4654.96, -139.1) * mm});
            skLineSegment(sketch, "E235.bottom", {"start": v(-4667.66, 0.6) * mm, "end": v(-4654.96, 0.6) * mm});
            skLineSegment(sketch, "E235.top", {"start": v(-4667.66, 13.3) * mm, "end": v(-4654.96, 13.3) * mm});
            skLineSegment(sketch, "E235.left", {"start": v(-4667.66, 0.6) * mm, "end": v(-4667.66, 13.3) * mm});
            skLineSegment(sketch, "E235.right", {"start": v(-4654.96, 0.6) * mm, "end": v(-4654.96, 13.3) * mm});
            skLineSegment(sketch, "E236.bottom", {"start": v(-4667.66, 153) * mm, "end": v(-4654.96, 153) * mm});
            skLineSegment(sketch, "E236.top", {"start": v(-4667.66, 165.7) * mm, "end": v(-4654.96, 165.7) * mm});
            skLineSegment(sketch, "E236.left", {"start": v(-4667.66, 153) * mm, "end": v(-4667.66, 165.7) * mm});
            skLineSegment(sketch, "E236.right", {"start": v(-4654.96, 153) * mm, "end": v(-4654.96, 165.7) * mm});
            skLineSegment(sketch, "E237.bottom", {"start": v(-4667.66, 305.4) * mm, "end": v(-4654.96, 305.4) * mm});
            skLineSegment(sketch, "E237.top", {"start": v(-4667.66, 318.1) * mm, "end": v(-4654.96, 318.1) * mm});
            skLineSegment(sketch, "E237.left", {"start": v(-4667.66, 305.4) * mm, "end": v(-4667.66, 318.1) * mm});
            skLineSegment(sketch, "E237.right", {"start": v(-4654.96, 305.4) * mm, "end": v(-4654.96, 318.1) * mm});
            skLineSegment(sketch, "E238.bottom", {"start": v(-4667.66, 457.8) * mm, "end": v(-4654.96, 457.8) * mm});
            skLineSegment(sketch, "E238.top", {"start": v(-4667.66, 470.5) * mm, "end": v(-4654.96, 470.5) * mm});
            skLineSegment(sketch, "E238.left", {"start": v(-4667.66, 457.8) * mm, "end": v(-4667.66, 470.5) * mm});
            skLineSegment(sketch, "E238.right", {"start": v(-4654.96, 457.8) * mm, "end": v(-4654.96, 470.5) * mm});
            skLineSegment(sketch, "E239.bottom", {"start": v(-2407.06, 584.8) * mm, "end": v(-2419.76, 584.8) * mm});
            skLineSegment(sketch, "E239.top", {"start": v(-2407.06, 572.1) * mm, "end": v(-2419.76, 572.1) * mm});
            skLineSegment(sketch, "E239.left", {"start": v(-2407.06, 584.8) * mm, "end": v(-2407.06, 572.1) * mm});
            skLineSegment(sketch, "E239.right", {"start": v(-2419.76, 584.8) * mm, "end": v(-2419.76, 572.1) * mm});
            skLineSegment(sketch, "E240.bottom", {"start": v(-2407.06, 432.4) * mm, "end": v(-2419.76, 432.4) * mm});
            skLineSegment(sketch, "E240.top", {"start": v(-2407.06, 419.7) * mm, "end": v(-2419.76, 419.7) * mm});
            skLineSegment(sketch, "E240.left", {"start": v(-2407.06, 432.4) * mm, "end": v(-2407.06, 419.7) * mm});
            skLineSegment(sketch, "E240.right", {"start": v(-2419.76, 432.4) * mm, "end": v(-2419.76, 419.7) * mm});
            skLineSegment(sketch, "E241.bottom", {"start": v(-2407.06, 280) * mm, "end": v(-2419.76, 280) * mm});
            skLineSegment(sketch, "E241.top", {"start": v(-2407.06, 267.3) * mm, "end": v(-2419.76, 267.3) * mm});
            skLineSegment(sketch, "E241.left", {"start": v(-2407.06, 280) * mm, "end": v(-2407.06, 267.3) * mm});
            skLineSegment(sketch, "E241.right", {"start": v(-2419.76, 280) * mm, "end": v(-2419.76, 267.3) * mm});
            skLineSegment(sketch, "E242.bottom", {"start": v(-2407.06, 127.6) * mm, "end": v(-2419.76, 127.6) * mm});
            skLineSegment(sketch, "E242.top", {"start": v(-2407.06, 114.9) * mm, "end": v(-2419.76, 114.9) * mm});
            skLineSegment(sketch, "E242.left", {"start": v(-2407.06, 127.6) * mm, "end": v(-2407.06, 114.9) * mm});
            skLineSegment(sketch, "E242.right", {"start": v(-2419.76, 127.6) * mm, "end": v(-2419.76, 114.9) * mm});
            skLineSegment(sketch, "E243.bottom", {"start": v(-2407.06, -24.8) * mm, "end": v(-2419.76, -24.8) * mm});
            skLineSegment(sketch, "E243.top", {"start": v(-2407.06, -37.5) * mm, "end": v(-2419.76, -37.5) * mm});
            skLineSegment(sketch, "E243.left", {"start": v(-2407.06, -24.8) * mm, "end": v(-2407.06, -37.5) * mm});
            skLineSegment(sketch, "E243.right", {"start": v(-2419.76, -24.8) * mm, "end": v(-2419.76, -37.5) * mm});
            skLineSegment(sketch, "E244.bottom", {"start": v(-4654.96, -139.1) * mm, "end": v(-2419.76, -139.1) * mm});
            skLineSegment(sketch, "E244.top", {"start": v(-4654.96, -37.5) * mm, "end": v(-2419.76, -37.5) * mm});
            skLineSegment(sketch, "E244.left", {"start": v(-4654.96, -139.1) * mm, "end": v(-4654.96, -37.5) * mm});
            skLineSegment(sketch, "E244.right", {"start": v(-2419.76, -139.1) * mm, "end": v(-2419.76, -37.5) * mm});
            skLineSegment(sketch, "E245.bottom", {"start": v(-2419.76, 114.9) * mm, "end": v(-4654.96, 114.9) * mm});
            skLineSegment(sketch, "E245.top", {"start": v(-2419.76, 13.3) * mm, "end": v(-4654.96, 13.3) * mm});
            skLineSegment(sketch, "E245.left", {"start": v(-2419.76, 114.9) * mm, "end": v(-2419.76, 13.3) * mm});
            skLineSegment(sketch, "E245.right", {"start": v(-4654.96, 114.9) * mm, "end": v(-4654.96, 13.3) * mm});
            skLineSegment(sketch, "E246.bottom", {"start": v(-4654.96, 165.7) * mm, "end": v(-2419.76, 165.7) * mm});
            skLineSegment(sketch, "E246.top", {"start": v(-4654.96, 267.3) * mm, "end": v(-2419.76, 267.3) * mm});
            skLineSegment(sketch, "E246.left", {"start": v(-4654.96, 165.7) * mm, "end": v(-4654.96, 267.3) * mm});
            skLineSegment(sketch, "E246.right", {"start": v(-2419.76, 165.7) * mm, "end": v(-2419.76, 267.3) * mm});
            skLineSegment(sketch, "E247.bottom", {"start": v(-2419.76, 419.7) * mm, "end": v(-4654.96, 419.7) * mm});
            skLineSegment(sketch, "E247.top", {"start": v(-2419.76, 318.1) * mm, "end": v(-4654.96, 318.1) * mm});
            skLineSegment(sketch, "E247.left", {"start": v(-2419.76, 419.7) * mm, "end": v(-2419.76, 318.1) * mm});
            skLineSegment(sketch, "E247.right", {"start": v(-4654.96, 419.7) * mm, "end": v(-4654.96, 318.1) * mm});
            skLineSegment(sketch, "E248.bottom", {"start": v(-4654.96, 470.5) * mm, "end": v(-2419.76, 470.5) * mm});
            skLineSegment(sketch, "E248.top", {"start": v(-4654.96, 572.1) * mm, "end": v(-2419.76, 572.1) * mm});
            skLineSegment(sketch, "E248.left", {"start": v(-4654.96, 470.5) * mm, "end": v(-4654.96, 572.1) * mm});
            skLineSegment(sketch, "E248.right", {"start": v(-2419.76, 470.5) * mm, "end": v(-2419.76, 572.1) * mm});
            skLineSegment(sketch, "E249.bottom", {"start": v(-2254.66, 635.6) * mm, "end": v(-2267.36, 635.6) * mm});
            skLineSegment(sketch, "E249.top", {"start": v(-2254.66, 622.9) * mm, "end": v(-2267.36, 622.9) * mm});
            skLineSegment(sketch, "E249.left", {"start": v(-2254.66, 635.6) * mm, "end": v(-2254.66, 622.9) * mm});
            skLineSegment(sketch, "E249.right", {"start": v(-2267.36, 635.6) * mm, "end": v(-2267.36, 622.9) * mm});
            skLineSegment(sketch, "E250.bottom", {"start": v(-2381.66, -664.08) * mm, "end": v(-2368.96, -664.08) * mm});
            skLineSegment(sketch, "E250.top", {"start": v(-2381.66, -651.38) * mm, "end": v(-2368.96, -651.38) * mm});
            skLineSegment(sketch, "E250.left", {"start": v(-2381.66, -664.08) * mm, "end": v(-2381.66, -651.38) * mm});
            skLineSegment(sketch, "E250.right", {"start": v(-2368.96, -664.08) * mm, "end": v(-2368.96, -651.38) * mm});
            skLineSegment(sketch, "E251.bottom", {"start": v(-2368.96, -651.38) * mm, "end": v(-2267.36, -651.38) * mm});
            skLineSegment(sketch, "E251.top", {"start": v(-2368.96, 622.9) * mm, "end": v(-2267.36, 622.9) * mm});
            skLineSegment(sketch, "E251.left", {"start": v(-2368.96, -651.38) * mm, "end": v(-2368.96, 622.9) * mm});
            skLineSegment(sketch, "E251.right", {"start": v(-2267.36, -651.38) * mm, "end": v(-2267.36, 622.9) * mm});
            skLineSegment(sketch, "E252.bottom", {"start": v(-2229.26, -151.8) * mm, "end": v(-2216.56, -151.8) * mm});
            skLineSegment(sketch, "E252.top", {"start": v(-2229.26, -139.1) * mm, "end": v(-2216.56, -139.1) * mm});
            skLineSegment(sketch, "E252.left", {"start": v(-2229.26, -151.8) * mm, "end": v(-2229.26, -139.1) * mm});
            skLineSegment(sketch, "E252.right", {"start": v(-2216.56, -151.8) * mm, "end": v(-2216.56, -139.1) * mm});
            skLineSegment(sketch, "E253.bottom", {"start": v(-2229.26, 0.6) * mm, "end": v(-2216.56, 0.6) * mm});
            skLineSegment(sketch, "E253.top", {"start": v(-2229.26, 13.3) * mm, "end": v(-2216.56, 13.3) * mm});
            skLineSegment(sketch, "E253.left", {"start": v(-2229.26, 0.6) * mm, "end": v(-2229.26, 13.3) * mm});
            skLineSegment(sketch, "E253.right", {"start": v(-2216.56, 0.6) * mm, "end": v(-2216.56, 13.3) * mm});
            skLineSegment(sketch, "E254.bottom", {"start": v(-2229.26, 153) * mm, "end": v(-2216.56, 153) * mm});
            skLineSegment(sketch, "E254.top", {"start": v(-2229.26, 165.7) * mm, "end": v(-2216.56, 165.7) * mm});
            skLineSegment(sketch, "E254.left", {"start": v(-2229.26, 153) * mm, "end": v(-2229.26, 165.7) * mm});
            skLineSegment(sketch, "E254.right", {"start": v(-2216.56, 153) * mm, "end": v(-2216.56, 165.7) * mm});
            skLineSegment(sketch, "E255.bottom", {"start": v(-2229.26, 305.4) * mm, "end": v(-2216.56, 305.4) * mm});
            skLineSegment(sketch, "E255.top", {"start": v(-2229.26, 318.1) * mm, "end": v(-2216.56, 318.1) * mm});
            skLineSegment(sketch, "E255.left", {"start": v(-2229.26, 305.4) * mm, "end": v(-2229.26, 318.1) * mm});
            skLineSegment(sketch, "E255.right", {"start": v(-2216.56, 305.4) * mm, "end": v(-2216.56, 318.1) * mm});
            skLineSegment(sketch, "E256.bottom", {"start": v(-2229.26, 457.8) * mm, "end": v(-2216.56, 457.8) * mm});
            skLineSegment(sketch, "E256.top", {"start": v(-2229.26, 470.5) * mm, "end": v(-2216.56, 470.5) * mm});
            skLineSegment(sketch, "E256.left", {"start": v(-2229.26, 457.8) * mm, "end": v(-2229.26, 470.5) * mm});
            skLineSegment(sketch, "E256.right", {"start": v(-2216.56, 457.8) * mm, "end": v(-2216.56, 470.5) * mm});
            skLineSegment(sketch, "E257.bottom", {"start": v(56.74, 584.8) * mm, "end": v(44.04, 584.8) * mm});
            skLineSegment(sketch, "E257.top", {"start": v(56.74, 572.1) * mm, "end": v(44.04, 572.1) * mm});
            skLineSegment(sketch, "E257.left", {"start": v(56.74, 584.8) * mm, "end": v(56.74, 572.1) * mm});
            skLineSegment(sketch, "E257.right", {"start": v(44.04, 584.8) * mm, "end": v(44.04, 572.1) * mm});
            skLineSegment(sketch, "E258.bottom", {"start": v(-95.66, 432.4) * mm, "end": v(-108.36, 432.4) * mm});
            skLineSegment(sketch, "E258.top", {"start": v(-95.66, 419.7) * mm, "end": v(-108.36, 419.7) * mm});
            skLineSegment(sketch, "E258.left", {"start": v(-95.66, 432.4) * mm, "end": v(-95.66, 419.7) * mm});
            skLineSegment(sketch, "E258.right", {"start": v(-108.36, 432.4) * mm, "end": v(-108.36, 419.7) * mm});
            skLineSegment(sketch, "E259.bottom", {"start": v(-248.06, 280) * mm, "end": v(-260.76, 280) * mm});
            skLineSegment(sketch, "E259.top", {"start": v(-248.06, 267.3) * mm, "end": v(-260.76, 267.3) * mm});
            skLineSegment(sketch, "E259.left", {"start": v(-248.06, 280) * mm, "end": v(-248.06, 267.3) * mm});
            skLineSegment(sketch, "E259.right", {"start": v(-260.76, 280) * mm, "end": v(-260.76, 267.3) * mm});
            skLineSegment(sketch, "E260.bottom", {"start": v(-400.46, 127.6) * mm, "end": v(-413.16, 127.6) * mm});
            skLineSegment(sketch, "E260.top", {"start": v(-400.46, 114.9) * mm, "end": v(-413.16, 114.9) * mm});
            skLineSegment(sketch, "E260.left", {"start": v(-400.46, 127.6) * mm, "end": v(-400.46, 114.9) * mm});
            skLineSegment(sketch, "E260.right", {"start": v(-413.16, 127.6) * mm, "end": v(-413.16, 114.9) * mm});
            skLineSegment(sketch, "E261.bottom", {"start": v(-552.86, -24.8) * mm, "end": v(-565.56, -24.8) * mm});
            skLineSegment(sketch, "E261.top", {"start": v(-552.86, -37.5) * mm, "end": v(-565.56, -37.5) * mm});
            skLineSegment(sketch, "E261.left", {"start": v(-552.86, -24.8) * mm, "end": v(-552.86, -37.5) * mm});
            skLineSegment(sketch, "E261.right", {"start": v(-565.56, -24.8) * mm, "end": v(-565.56, -37.5) * mm});
            skLineSegment(sketch, "E262.bottom", {"start": v(-679.86, -609) * mm, "end": v(-667.16, -609) * mm});
            skLineSegment(sketch, "E262.top", {"start": v(-679.86, -596.3) * mm, "end": v(-667.16, -596.3) * mm});
            skLineSegment(sketch, "E262.left", {"start": v(-679.86, -609) * mm, "end": v(-679.86, -596.3) * mm});
            skLineSegment(sketch, "E262.right", {"start": v(-667.16, -609) * mm, "end": v(-667.16, -596.3) * mm});
            skLineSegment(sketch, "E263.bottom", {"start": v(-375.06, -664.08) * mm, "end": v(-362.36, -664.08) * mm});
            skLineSegment(sketch, "E263.top", {"start": v(-375.06, -651.38) * mm, "end": v(-362.36, -651.38) * mm});
            skLineSegment(sketch, "E263.left", {"start": v(-375.06, -664.08) * mm, "end": v(-375.06, -651.38) * mm});
            skLineSegment(sketch, "E263.right", {"start": v(-362.36, -664.08) * mm, "end": v(-362.36, -651.38) * mm});
            skLineSegment(sketch, "E264.bottom", {"start": v(-70.26, -752.63) * mm, "end": v(-57.56, -752.63) * mm});
            skLineSegment(sketch, "E264.top", {"start": v(-70.26, -739.93) * mm, "end": v(-57.56, -739.93) * mm});
            skLineSegment(sketch, "E264.left", {"start": v(-70.26, -752.63) * mm, "end": v(-70.26, -739.93) * mm});
            skLineSegment(sketch, "E264.right", {"start": v(-57.56, -752.63) * mm, "end": v(-57.56, -739.93) * mm});
            skLineSegment(sketch, "E265.bottom", {"start": v(-57.56, -739.93) * mm, "end": v(44.04, -739.93) * mm});
            skLineSegment(sketch, "E265.top", {"start": v(-57.56, 572.1) * mm, "end": v(44.04, 572.1) * mm});
            skLineSegment(sketch, "E265.left", {"start": v(-57.56, -739.93) * mm, "end": v(-57.56, 572.1) * mm});
            skLineSegment(sketch, "E265.right", {"start": v(44.04, -739.93) * mm, "end": v(44.04, 572.1) * mm});
            skLineSegment(sketch, "E266.bottom", {"start": v(-260.76, 267.3) * mm, "end": v(-362.36, 267.3) * mm});
            skLineSegment(sketch, "E266.top", {"start": v(-260.76, -651.38) * mm, "end": v(-362.36, -651.38) * mm});
            skLineSegment(sketch, "E266.left", {"start": v(-260.76, 267.3) * mm, "end": v(-260.76, -651.38) * mm});
            skLineSegment(sketch, "E266.right", {"start": v(-362.36, 267.3) * mm, "end": v(-362.36, -651.38) * mm});
            skLineSegment(sketch, "E267.bottom", {"start": v(-260.76, 267.3) * mm, "end": v(-2216.56, 267.3) * mm});
            skLineSegment(sketch, "E267.top", {"start": v(-260.76, 165.7) * mm, "end": v(-2216.56, 165.7) * mm});
            skLineSegment(sketch, "E267.left", {"start": v(-260.76, 267.3) * mm, "end": v(-260.76, 165.7) * mm});
            skLineSegment(sketch, "E267.right", {"start": v(-2216.56, 267.3) * mm, "end": v(-2216.56, 165.7) * mm});
            skLineSegment(sketch, "E268.bottom", {"start": v(-2216.56, -139.1) * mm, "end": v(-565.56, -139.1) * mm});
            skLineSegment(sketch, "E268.top", {"start": v(-2216.56, -37.5) * mm, "end": v(-565.56, -37.5) * mm});
            skLineSegment(sketch, "E268.left", {"start": v(-2216.56, -139.1) * mm, "end": v(-2216.56, -37.5) * mm});
            skLineSegment(sketch, "E268.right", {"start": v(-565.56, -139.1) * mm, "end": v(-565.56, -37.5) * mm});
            skLineSegment(sketch, "E269.bottom", {"start": v(-565.56, -37.5) * mm, "end": v(-667.16, -37.5) * mm});
            skLineSegment(sketch, "E269.top", {"start": v(-565.56, -596.3) * mm, "end": v(-667.16, -596.3) * mm});
            skLineSegment(sketch, "E269.left", {"start": v(-565.56, -37.5) * mm, "end": v(-565.56, -596.3) * mm});
            skLineSegment(sketch, "E269.right", {"start": v(-667.16, -37.5) * mm, "end": v(-667.16, -596.3) * mm});
            skLineSegment(sketch, "E270.bottom", {"start": v(44.04, 572.1) * mm, "end": v(-2216.56, 572.1) * mm});
            skLineSegment(sketch, "E270.top", {"start": v(44.04, 470.5) * mm, "end": v(-2216.56, 470.5) * mm});
            skLineSegment(sketch, "E270.left", {"start": v(44.04, 572.1) * mm, "end": v(44.04, 470.5) * mm});
            skLineSegment(sketch, "E270.right", {"start": v(-2216.56, 572.1) * mm, "end": v(-2216.56, 470.5) * mm});
            skLineSegment(sketch, "E271.bottom", {"start": v(-4820.06, 635.6) * mm, "end": v(-4807.36, 635.6) * mm});
            skLineSegment(sketch, "E271.top", {"start": v(-4820.06, 622.9) * mm, "end": v(-4807.36, 622.9) * mm});
            skLineSegment(sketch, "E271.left", {"start": v(-4820.06, 635.6) * mm, "end": v(-4820.06, 622.9) * mm});
            skLineSegment(sketch, "E272", {"start": v(-4807.36, 635.6) * mm, "end": v(-4807.36, 622.9) * mm});
            skLineSegment(sketch, "E273.bottom", {"start": v(-4693.06, -638.68) * mm, "end": v(-4705.76, -638.68) * mm});
            skLineSegment(sketch, "E273.top", {"start": v(-4693.06, -625.98) * mm, "end": v(-4705.76, -625.98) * mm});
            skLineSegment(sketch, "E273.left", {"start": v(-4693.06, -638.68) * mm, "end": v(-4693.06, -625.98) * mm});
            skLineSegment(sketch, "E273.right", {"start": v(-4705.76, -638.68) * mm, "end": v(-4705.76, -625.98) * mm});
            skLineSegment(sketch, "E274.bottom", {"start": v(-4705.76, -625.98) * mm, "end": v(-4807.36, -625.98) * mm});
            skLineSegment(sketch, "E274.top", {"start": v(-4705.76, 622.9) * mm, "end": v(-4807.36, 622.9) * mm});
            skLineSegment(sketch, "E274.left", {"start": v(-4705.76, -625.98) * mm, "end": v(-4705.76, 622.9) * mm});
            skLineSegment(sketch, "E274.right", {"start": v(-4807.36, -625.98) * mm, "end": v(-4807.36, 622.9) * mm});
            skLineSegment(sketch, "E275.MirrorCS", {"start": v(1872.84, 572.1) * mm, "end": v(1771.24, 572.1) * mm});
            skLineSegment(sketch, "E276.MirrorCS", {"start": v(1771.24, 572.1) * mm, "end": v(4031.84, 572.1) * mm});
            skLineSegment(sketch, "E277.MirrorCS", {"start": v(1771.24, -739.93) * mm, "end": v(1771.24, 572.1) * mm});
            skLineSegment(sketch, "E278.MirrorCS", {"start": v(1872.84, -739.93) * mm, "end": v(1872.84, 572.1) * mm});
            skLineSegment(sketch, "E279.MirrorCS", {"start": v(1771.24, 470.5) * mm, "end": v(4031.84, 470.5) * mm});
            skLineSegment(sketch, "E280.MirrorCS", {"start": v(1872.84, -739.93) * mm, "end": v(1771.24, -739.93) * mm});
            skLineSegment(sketch, "E281.MirrorCS", {"start": v(2076.04, -651.38) * mm, "end": v(2177.64, -651.38) * mm});
            skLineSegment(sketch, "E282.MirrorCS", {"start": v(2380.84, -596.3) * mm, "end": v(2482.44, -596.3) * mm});
            skLineSegment(sketch, "E283.MirrorCS", {"start": v(2380.84, -37.5) * mm, "end": v(2380.84, -596.3) * mm});
            skLineSegment(sketch, "E284.MirrorCS", {"start": v(2482.44, -37.5) * mm, "end": v(2482.44, -596.3) * mm});
            skLineSegment(sketch, "E285.MirrorCS", {"start": v(2177.64, 267.3) * mm, "end": v(2177.64, -651.38) * mm});
            skLineSegment(sketch, "E286.MirrorCS", {"start": v(2076.04, 267.3) * mm, "end": v(2076.04, -651.38) * mm});
            skLineSegment(sketch, "E287.MirrorCS", {"start": v(2076.04, 267.3) * mm, "end": v(2076.04, 165.7) * mm});
            skLineSegment(sketch, "E288.MirrorCS", {"start": v(2076.04, 267.3) * mm, "end": v(4031.84, 267.3) * mm});
            skLineSegment(sketch, "E289.MirrorCS", {"start": v(2076.04, 165.7) * mm, "end": v(4031.84, 165.7) * mm});
            skLineSegment(sketch, "E290.MirrorCS", {"start": v(2380.84, -37.5) * mm, "end": v(2482.44, -37.5) * mm});
            skLineSegment(sketch, "E291.MirrorCS", {"start": v(4031.84, -37.5) * mm, "end": v(2380.84, -37.5) * mm});
            skLineSegment(sketch, "E292.MirrorCS", {"start": v(4031.84, -139.1) * mm, "end": v(2380.84, -139.1) * mm});
            skLineSegment(sketch, "E293.MirrorCS", {"start": v(4031.84, -139.1) * mm, "end": v(4031.84, -37.5) * mm});
            skLineSegment(sketch, "E294.MirrorCS", {"start": v(4031.84, 267.3) * mm, "end": v(4031.84, 165.7) * mm});
            skLineSegment(sketch, "E295.MirrorCS", {"start": v(4031.84, 572.1) * mm, "end": v(4031.84, 470.5) * mm});
            skLineSegment(sketch, "E296.MirrorCS", {"start": v(4184.24, -651.38) * mm, "end": v(4082.64, -651.38) * mm});
            skLineSegment(sketch, "E297.MirrorCS", {"start": v(4184.24, -651.38) * mm, "end": v(4184.24, 622.9) * mm});
            skLineSegment(sketch, "E298.MirrorCS", {"start": v(4082.64, -651.38) * mm, "end": v(4082.64, 622.9) * mm});
            skLineSegment(sketch, "E299.MirrorCS", {"start": v(4184.24, 622.9) * mm, "end": v(4082.64, 622.9) * mm});
            skLineSegment(sketch, "E300.MirrorCS", {"start": v(4235.04, 470.5) * mm, "end": v(4235.04, 572.1) * mm});
            skLineSegment(sketch, "E301.MirrorCS", {"start": v(4235.04, 419.7) * mm, "end": v(4235.04, 318.1) * mm});
            skLineSegment(sketch, "E302.MirrorCS", {"start": v(4235.04, 165.7) * mm, "end": v(4235.04, 267.3) * mm});
            skLineSegment(sketch, "E303.MirrorCS", {"start": v(4235.04, 114.9) * mm, "end": v(4235.04, 13.3) * mm});
            skLineSegment(sketch, "E304.MirrorCS", {"start": v(4235.04, -139.1) * mm, "end": v(4235.04, -37.5) * mm});
            skLineSegment(sketch, "E305.MirrorCS", {"start": v(6470.24, -37.5) * mm, "end": v(4235.04, -37.5) * mm});
            skLineSegment(sketch, "E306.MirrorCS", {"start": v(6470.24, -139.1) * mm, "end": v(4235.04, -139.1) * mm});
            skLineSegment(sketch, "E307.MirrorCS", {"start": v(6470.24, 267.3) * mm, "end": v(4235.04, 267.3) * mm});
            skLineSegment(sketch, "E308.MirrorCS", {"start": v(6470.24, 470.5) * mm, "end": v(4235.04, 470.5) * mm});
            skLineSegment(sketch, "E309.MirrorCS", {"start": v(6470.24, 572.1) * mm, "end": v(4235.04, 572.1) * mm});
            skLineSegment(sketch, "E310.MirrorCS", {"start": v(6470.24, 470.5) * mm, "end": v(6470.24, 572.1) * mm});
            skLineSegment(sketch, "E311.MirrorCS", {"start": v(6470.24, 165.7) * mm, "end": v(6470.24, 267.3) * mm});
            skLineSegment(sketch, "E312.MirrorCS", {"start": v(6470.24, -139.1) * mm, "end": v(6470.24, -37.5) * mm});
            skLineSegment(sketch, "E313.MirrorCS", {"start": v(6673.44, -139.1) * mm, "end": v(6673.44, -37.5) * mm});
            skLineSegment(sketch, "E314.MirrorCS", {"start": v(6978.24, -37.5) * mm, "end": v(6673.44, -37.5) * mm});
            skLineSegment(sketch, "E315.MirrorCS", {"start": v(6673.44, -139.1) * mm, "end": v(7054.44, -139.1) * mm});
            skLineSegment(sketch, "E316.MirrorCS", {"start": v(7054.44, 572.1) * mm, "end": v(7054.44, -139.1) * mm});
            skLineSegment(sketch, "E317.MirrorCS", {"start": v(6978.24, 457.8) * mm, "end": v(6978.24, -37.5) * mm});
            skLineSegment(sketch, "E318.MirrorCS", {"start": v(6927.44, 419.7) * mm, "end": v(6927.44, 13.3) * mm});
            skLineSegment(sketch, "E319.MirrorCS", {"start": v(6673.44, 13.3) * mm, "end": v(6673.44, 114.9) * mm});
            skLineSegment(sketch, "E320.MirrorCS", {"start": v(6813.14, 114.9) * mm, "end": v(6673.44, 114.9) * mm});
            skLineSegment(sketch, "E321.MirrorCS", {"start": v(6825.84, 127.6) * mm, "end": v(6825.84, 318.1) * mm});
            skLineSegment(sketch, "E322.MirrorCS", {"start": v(6673.44, 318.1) * mm, "end": v(6813.14, 318.1) * mm});
            skLineSegment(sketch, "E323.MirrorCS", {"start": v(6673.44, 419.7) * mm, "end": v(6673.44, 318.1) * mm});
            skLineSegment(sketch, "E324.MirrorCS", {"start": v(6673.44, 419.7) * mm, "end": v(6927.44, 419.7) * mm});
            skLineSegment(sketch, "E325.MirrorCS", {"start": v(6775.04, 267.3) * mm, "end": v(6673.44, 267.3) * mm});
            skLineSegment(sketch, "E326.MirrorCS", {"start": v(6775.04, 165.7) * mm, "end": v(6775.04, 267.3) * mm});
            skLineSegment(sketch, "E327.MirrorCS", {"start": v(6775.04, 165.7) * mm, "end": v(6673.44, 165.7) * mm});
            skLineSegment(sketch, "E328.MirrorCS", {"start": v(6673.44, 165.7) * mm, "end": v(6673.44, 267.3) * mm});
            skLineSegment(sketch, "E329.MirrorCS", {"start": v(7054.44, 572.1) * mm, "end": v(6673.44, 572.1) * mm});
            skLineSegment(sketch, "E330", {"start": v(6674.46, 474.04) * mm, "end": v(6978.24, 474.04) * mm});
            skLineSegment(sketch, "E331", {"start": v(6978.24, 474.04) * mm, "end": v(6978.24, 457.8) * mm});
            skLineSegment(sketch, "E332", {"start": v(6674.46, 474.04) * mm, "end": v(6673.44, 572.1) * mm});
            skLineSegment(sketch, "E333", {"start": v(6673.44, 13.3) * mm, "end": v(6927.44, 13.3) * mm});
            skLineSegment(sketch, "E334", {"start": v(6813.14, 318.1) * mm, "end": v(6825.84, 318.1) * mm});
            skLineSegment(sketch, "E335", {"start": v(6470.24, 165.7) * mm, "end": v(4235.04, 165.7) * mm});
            skLineSegment(sketch, "E336.MirrorCS", {"start": v(6622.64, -625.98) * mm, "end": v(6622.64, 622.9) * mm});
            skLineSegment(sketch, "E337.MirrorCS", {"start": v(6521.04, -625.98) * mm, "end": v(6622.64, -625.98) * mm});
            skLineSegment(sketch, "E338.MirrorCS", {"start": v(6521.04, -625.98) * mm, "end": v(6521.04, 622.9) * mm});
            skLineSegment(sketch, "E339.MirrorCS", {"start": v(6521.04, 622.9) * mm, "end": v(6622.64, 622.9) * mm});
            skLineSegment(sketch, "E340", {"start": v(6673.44, 114.9) * mm, "end": v(6673.44, 127.6) * mm});
            skLineSegment(sketch, "E341", {"start": v(6673.44, 13.3) * mm, "end": v(6673.44, 0.6) * mm});
            skLineSegment(sketch, "E342", {"start": v(6673.44, 318.1) * mm, "end": v(6673.44, 305.4) * mm});
            skLineSegment(sketch, "E343", {"start": v(6673.44, 419.7) * mm, "end": v(6673.44, 432.4) * mm});
            skLineSegment(sketch, "E344", {"start": v(6825.84, 127.6) * mm, "end": v(6825.84, 114.9) * mm});
            skLineSegment(sketch, "E345", {"start": v(6813.14, 114.9) * mm, "end": v(6825.84, 114.9) * mm});
            skSolve(sketch);
        }
        {
            var Q0;
            Q0=makeQuery(id+"F0.imprint","IMPRINT",FACE,{"disambiguationData":[TD([[makeQuery(id+"F0.imprint","IMPRINT",EDGE,{"derivedFrom":sQuery(id+"F0.wireOp",EDGE,"E214.top")}),-1.0]])]});
            var Q1;
            Q1=makeQuery(id+"F0.imprint","IMPRINT",FACE,{"disambiguationData":[TD([[makeQuery(id+"F0.imprint","IMPRINT",EDGE,{"derivedFrom":sQuery(id+"F0.wireOp",EDGE,"E226.bottom")}),1.0]])]});
            var Q2;
            {var subQ5=sQuery(id+"F0.wireOp",EDGE,"E274.top");Q2=makeQuery(id+"F0.imprint","IMPRINT",FACE,{"disambiguationData":[TD([[makeQuery(id+"F0.imprint","IMPRINT",EDGE,{"derivedFrom":subQ5}),1.0]])]});}
            var Q3;
            Q3=makeQuery(id+"F0.imprint","IMPRINT",FACE,{"disambiguationData":[TD([[makeQuery(id+"F0.imprint","IMPRINT",EDGE,{"derivedFrom":sQuery(id+"F0.wireOp",EDGE,"E248.bottom")}),1.0]])]});
            var Q4;
            Q4=makeQuery(id+"F0.imprint","IMPRINT",FACE,{"disambiguationData":[TD([[makeQuery(id+"F0.imprint","IMPRINT",EDGE,{"derivedFrom":sQuery(id+"F0.wireOp",EDGE,"E246.bottom")}),1.0]])]});
            var Q5;
            {var subQ5=sQuery(id+"F0.wireOp",EDGE,"E244.top");Q5=makeQuery(id+"F0.imprint","IMPRINT",FACE,{"disambiguationData":[TD([[makeQuery(id+"F0.imprint","IMPRINT",EDGE,{"derivedFrom":subQ5}),-1.0]])]});}
            var Q6;
            {var subQ5=sQuery(id+"F0.wireOp",EDGE,"E244.bottom");Q6=makeQuery(id+"F0.imprint","IMPRINT",FACE,{"disambiguationData":[TD([[makeQuery(id+"F0.imprint","IMPRINT",EDGE,{"derivedFrom":subQ5}),1.0]])]});}
            var Q7;
            {var subQ5=sQuery(id+"F0.wireOp",EDGE,"E216");Q7=makeQuery(id+"F0.imprint","IMPRINT",FACE,{"disambiguationData":[TD([[makeQuery(id+"F0.imprint","IMPRINT",EDGE,{"derivedFrom":subQ5}),-1.0]])]});}
            var Q8;
            {var subQ5=sQuery(id+"F0.wireOp",EDGE,"E274.bottom");Q8=makeQuery(id+"F0.imprint","IMPRINT",FACE,{"disambiguationData":[TD([[makeQuery(id+"F0.imprint","IMPRINT",EDGE,{"derivedFrom":subQ5}),-1.0]])]});}
            var Q9;
            {var subQ5=sQuery(id+"F0.wireOp",EDGE,"E251.top");Q9=makeQuery(id+"F0.imprint","IMPRINT",FACE,{"disambiguationData":[TD([[makeQuery(id+"F0.imprint","IMPRINT",EDGE,{"derivedFrom":subQ5}),-1.0]])]});}
            var Q10;
            {var subQ5=sQuery(id+"F0.wireOp",EDGE,"E251.bottom");Q10=makeQuery(id+"F0.imprint","IMPRINT",FACE,{"disambiguationData":[TD([[makeQuery(id+"F0.imprint","IMPRINT",EDGE,{"derivedFrom":subQ5}),1.0]])]});}
            var Q11;
            {var subQ5=sQuery(id+"F0.wireOp",EDGE,"E268.top");Q11=makeQuery(id+"F0.imprint","IMPRINT",FACE,{"disambiguationData":[TD([[makeQuery(id+"F0.imprint","IMPRINT",EDGE,{"derivedFrom":subQ5}),-1.0]])]});}
            var Q12;
            {var subQ0=sQuery(id+"F0.wireOp",EDGE,"E268.left");var subQ1=sQuery(id+"F0.wireOp",EDGE,"E1");var subQ2=makeQuery(id+"F0.imprint","INTERSECT",VERTEX,{"derivedFrom":[subQ1,subQ0]});Q12=makeQuery(id+"F0.imprint","IMPRINT",FACE,{"disambiguationData":[TD([[makeQuery(id+"F0.imprint","IMPRINT",EDGE,{"disambiguationData":[TD([[subQ2,-1.0]])],"derivedFrom":subQ1}),-1.0]])]});}
            var Q13;
            {var subQ5=sQuery(id+"F0.wireOp",EDGE,"E267.right");Q13=makeQuery(id+"F0.imprint","IMPRINT",FACE,{"disambiguationData":[TD([[makeQuery(id+"F0.imprint","IMPRINT",EDGE,{"derivedFrom":subQ5}),1.0]])]});}
            var Q14;
            {var subQ5=sQuery(id+"F0.wireOp",EDGE,"E270.right");Q14=makeQuery(id+"F0.imprint","IMPRINT",FACE,{"disambiguationData":[TD([[makeQuery(id+"F0.imprint","IMPRINT",EDGE,{"derivedFrom":subQ5}),1.0]])]});}
            var Q15;
            {var subQ5=sQuery(id+"F0.wireOp",EDGE,"E269.bottom");Q15=makeQuery(id+"F0.imprint","IMPRINT",FACE,{"disambiguationData":[TD([[makeQuery(id+"F0.imprint","IMPRINT",EDGE,{"derivedFrom":subQ5}),1.0]])]});}
            var Q16;
            {var subQ0=sQuery(id+"F0.wireOp",EDGE,"E269.right");var subQ1=sQuery(id+"F0.wireOp",EDGE,"E1");var subQ2=makeQuery(id+"F0.imprint","INTERSECT",VERTEX,{"derivedFrom":[subQ1,subQ0]});Q16=makeQuery(id+"F0.imprint","IMPRINT",FACE,{"disambiguationData":[TD([[makeQuery(id+"F0.imprint","IMPRINT",EDGE,{"disambiguationData":[TD([[subQ2,-1.0]])],"derivedFrom":subQ1}),-1.0]])]});}
            var Q17;
            {var subQ5=sQuery(id+"F0.wireOp",EDGE,"E267.left");Q17=makeQuery(id+"F0.imprint","IMPRINT",FACE,{"disambiguationData":[TD([[makeQuery(id+"F0.imprint","IMPRINT",EDGE,{"derivedFrom":subQ5}),-1.0]])]});}
            var Q18;
            {var subQ5=sQuery(id+"F0.wireOp",EDGE,"E270.left");Q18=makeQuery(id+"F0.imprint","IMPRINT",FACE,{"disambiguationData":[TD([[makeQuery(id+"F0.imprint","IMPRINT",EDGE,{"derivedFrom":subQ5}),-1.0]])]});}
            var Q19;
            {var subQ0=sQuery(id+"F0.wireOp",EDGE,"E265.left");var subQ1=sQuery(id+"F0.wireOp",EDGE,"E1");var subQ2=makeQuery(id+"F0.imprint","INTERSECT",VERTEX,{"derivedFrom":[subQ1,subQ0]});Q19=makeQuery(id+"F0.imprint","IMPRINT",FACE,{"disambiguationData":[TD([[makeQuery(id+"F0.imprint","IMPRINT",EDGE,{"disambiguationData":[TD([[subQ2,-1.0]])],"derivedFrom":subQ1}),1.0]])]});}
            var Q20;
            {var subQ0=sQuery(id+"F0.wireOp",EDGE,"E266.right");var subQ1=sQuery(id+"F0.wireOp",EDGE,"E1");var subQ2=makeQuery(id+"F0.imprint","INTERSECT",VERTEX,{"derivedFrom":[subQ1,subQ0]});Q20=makeQuery(id+"F0.imprint","IMPRINT",FACE,{"disambiguationData":[TD([[makeQuery(id+"F0.imprint","IMPRINT",EDGE,{"disambiguationData":[TD([[subQ2,-1.0]])],"derivedFrom":subQ1}),1.0]])]});}
            var Q21;
            {var subQ5=sQuery(id+"F0.wireOp",EDGE,"E269.top");Q21=makeQuery(id+"F0.imprint","IMPRINT",FACE,{"disambiguationData":[TD([[makeQuery(id+"F0.imprint","IMPRINT",EDGE,{"derivedFrom":subQ5}),-1.0]])]});}
            var Q22;
            {var subQ5=sQuery(id+"F0.wireOp",EDGE,"E266.top");Q22=makeQuery(id+"F0.imprint","IMPRINT",FACE,{"disambiguationData":[TD([[makeQuery(id+"F0.imprint","IMPRINT",EDGE,{"derivedFrom":subQ5}),-1.0]])]});}
            var Q23;
            {var subQ5=sQuery(id+"F0.wireOp",EDGE,"E265.bottom");Q23=makeQuery(id+"F0.imprint","IMPRINT",FACE,{"disambiguationData":[TD([[makeQuery(id+"F0.imprint","IMPRINT",EDGE,{"derivedFrom":subQ5}),1.0]])]});}
            var Q24;
            {var subQ5=sQuery(id+"F0.wireOp",EDGE,"E287.MirrorCS");Q24=makeQuery(id+"F0.imprint","IMPRINT",FACE,{"disambiguationData":[TD([[makeQuery(id+"F0.imprint","IMPRINT",EDGE,{"derivedFrom":subQ5}),1.0]])]});}
            var Q25;
            {var subQ0=sQuery(id+"F0.wireOp",EDGE,"E286.MirrorCS");var subQ1=sQuery(id+"F0.wireOp",EDGE,"E1");var subQ2=makeQuery(id+"F0.imprint","INTERSECT",VERTEX,{"derivedFrom":[subQ1,subQ0]});Q25=makeQuery(id+"F0.imprint","IMPRINT",FACE,{"disambiguationData":[TD([[makeQuery(id+"F0.imprint","IMPRINT",EDGE,{"disambiguationData":[TD([[subQ2,-1.0]])],"derivedFrom":subQ1}),1.0]])]});}
            var Q26;
            {var subQ5=sQuery(id+"F0.wireOp",EDGE,"E281.MirrorCS");Q26=makeQuery(id+"F0.imprint","IMPRINT",FACE,{"disambiguationData":[TD([[makeQuery(id+"F0.imprint","IMPRINT",EDGE,{"derivedFrom":subQ5}),1.0]])]});}
            var Q27;
            {var subQ5=sQuery(id+"F0.wireOp",EDGE,"E294.MirrorCS");Q27=makeQuery(id+"F0.imprint","IMPRINT",FACE,{"disambiguationData":[TD([[makeQuery(id+"F0.imprint","IMPRINT",EDGE,{"derivedFrom":subQ5}),-1.0]])]});}
            var Q28;
            {var subQ0=sQuery(id+"F0.wireOp",EDGE,"E283.MirrorCS");var subQ1=sQuery(id+"F0.wireOp",EDGE,"E1");var subQ2=makeQuery(id+"F0.imprint","INTERSECT",VERTEX,{"derivedFrom":[subQ1,subQ0]});Q28=makeQuery(id+"F0.imprint","IMPRINT",FACE,{"disambiguationData":[TD([[makeQuery(id+"F0.imprint","IMPRINT",EDGE,{"disambiguationData":[TD([[subQ2,-1.0]])],"derivedFrom":subQ1}),1.0]])]});}
            var Q29;
            {var subQ0=sQuery(id+"F0.wireOp",EDGE,"E283.MirrorCS");var subQ1=sQuery(id+"F0.wireOp",EDGE,"E1");var subQ2=makeQuery(id+"F0.imprint","INTERSECT",VERTEX,{"derivedFrom":[subQ1,subQ0]});Q29=makeQuery(id+"F0.imprint","IMPRINT",FACE,{"disambiguationData":[TD([[makeQuery(id+"F0.imprint","IMPRINT",EDGE,{"disambiguationData":[TD([[subQ2,-1.0]])],"derivedFrom":subQ1}),-1.0]])]});}
            var Q30;
            {var subQ0=sQuery(id+"F0.wireOp",EDGE,"E282.MirrorCS");Q30=makeQuery(id+"F0.imprint","IMPRINT",FACE,{"disambiguationData":[TD([[makeQuery(id+"F0.imprint","IMPRINT",EDGE,{"derivedFrom":subQ0}),1.0]])]});}
            var Q31;
            {var subQ0=sQuery(id+"F0.wireOp",EDGE,"E284.MirrorCS");var subQ1=sQuery(id+"F0.wireOp",EDGE,"E1");var subQ2=makeQuery(id+"F0.imprint","INTERSECT",VERTEX,{"derivedFrom":[subQ1,subQ0]});Q31=makeQuery(id+"F0.imprint","IMPRINT",FACE,{"disambiguationData":[TD([[makeQuery(id+"F0.imprint","IMPRINT",EDGE,{"disambiguationData":[TD([[subQ2,-1.0]])],"derivedFrom":subQ1}),1.0]])]});}
            var Q32;
            {var subQ0=sQuery(id+"F0.wireOp",EDGE,"E284.MirrorCS");var subQ1=sQuery(id+"F0.wireOp",EDGE,"E1");var subQ2=makeQuery(id+"F0.imprint","INTERSECT",VERTEX,{"derivedFrom":[subQ1,subQ0]});Q32=makeQuery(id+"F0.imprint","IMPRINT",FACE,{"disambiguationData":[TD([[makeQuery(id+"F0.imprint","IMPRINT",EDGE,{"disambiguationData":[TD([[subQ2,-1.0]])],"derivedFrom":subQ1}),-1.0]])]});}
            var Q33;
            {var subQ0=sQuery(id+"F0.wireOp",EDGE,"E295.MirrorCS");Q33=makeQuery(id+"F0.imprint","IMPRINT",FACE,{"disambiguationData":[TD([[makeQuery(id+"F0.imprint","IMPRINT",EDGE,{"derivedFrom":subQ0}),-1.0]])]});}
            var Q34;
            {var subQ0=sQuery(id+"F0.wireOp",EDGE,"E277.MirrorCS");var subQ1=sQuery(id+"F0.wireOp",EDGE,"E276.MirrorCS");var subQ2=makeQuery(id+"F0.imprint","INTERSECT",VERTEX,{"derivedFrom":[subQ1,subQ0]});Q34=makeQuery(id+"F0.imprint","IMPRINT",FACE,{"disambiguationData":[TD([[makeQuery(id+"F0.imprint","IMPRINT",EDGE,{"disambiguationData":[TD([[subQ2,-1.0]])],"derivedFrom":subQ1}),-1.0]])]});}
            var Q35;
            {var subQ0=sQuery(id+"F0.wireOp",EDGE,"E277.MirrorCS");var subQ1=sQuery(id+"F0.wireOp",EDGE,"E1");var subQ2=makeQuery(id+"F0.imprint","INTERSECT",VERTEX,{"derivedFrom":[subQ1,subQ0]});Q35=makeQuery(id+"F0.imprint","IMPRINT",FACE,{"disambiguationData":[TD([[makeQuery(id+"F0.imprint","IMPRINT",EDGE,{"disambiguationData":[TD([[subQ2,-1.0]])],"derivedFrom":subQ1}),1.0]])]});}
            var Q36;
            {var subQ5=sQuery(id+"F0.wireOp",EDGE,"E280.MirrorCS");Q36=makeQuery(id+"F0.imprint","IMPRINT",FACE,{"disambiguationData":[TD([[makeQuery(id+"F0.imprint","IMPRINT",EDGE,{"derivedFrom":subQ5}),-1.0]])]});}
            var Q37;
            {var subQ5=sQuery(id+"F0.wireOp",EDGE,"E299.MirrorCS");Q37=makeQuery(id+"F0.imprint","IMPRINT",FACE,{"disambiguationData":[TD([[makeQuery(id+"F0.imprint","IMPRINT",EDGE,{"derivedFrom":subQ5}),1.0]])]});}
            var Q38;
            {var subQ5=sQuery(id+"F0.wireOp",EDGE,"E296.MirrorCS");Q38=makeQuery(id+"F0.imprint","IMPRINT",FACE,{"disambiguationData":[TD([[makeQuery(id+"F0.imprint","IMPRINT",EDGE,{"derivedFrom":subQ5}),-1.0]])]});}
            var Q39;
            Q39=makeQuery(id+"F0.imprint","IMPRINT",FACE,{"disambiguationData":[TD([[makeQuery(id+"F0.imprint","IMPRINT",EDGE,{"derivedFrom":sQuery(id+"F0.wireOp",EDGE,"E308.MirrorCS")}),-1.0]])]});
            var Q40;
            Q40=makeQuery(id+"F0.imprint","IMPRINT",FACE,{"disambiguationData":[TD([[makeQuery(id+"F0.imprint","IMPRINT",EDGE,{"derivedFrom":sQuery(id+"F0.wireOp",EDGE,"E302.MirrorCS")}),-1.0]])]});
            var Q41;
            {var subQ5=sQuery(id+"F0.wireOp",EDGE,"E305.MirrorCS");Q41=makeQuery(id+"F0.imprint","IMPRINT",FACE,{"disambiguationData":[TD([[makeQuery(id+"F0.imprint","IMPRINT",EDGE,{"derivedFrom":subQ5}),1.0]])]});}
            var Q42;
            {var subQ5=sQuery(id+"F0.wireOp",EDGE,"E306.MirrorCS");Q42=makeQuery(id+"F0.imprint","IMPRINT",FACE,{"disambiguationData":[TD([[makeQuery(id+"F0.imprint","IMPRINT",EDGE,{"derivedFrom":subQ5}),-1.0]])]});}
            var Q43;
            {var subQ5=sQuery(id+"F0.wireOp",EDGE,"E339.MirrorCS");Q43=makeQuery(id+"F0.imprint","IMPRINT",FACE,{"disambiguationData":[TD([[makeQuery(id+"F0.imprint","IMPRINT",EDGE,{"derivedFrom":subQ5}),-1.0]])]});}
            var Q44;
            {var subQ5=sQuery(id+"F0.wireOp",EDGE,"E337.MirrorCS");Q44=makeQuery(id+"F0.imprint","IMPRINT",FACE,{"disambiguationData":[TD([[makeQuery(id+"F0.imprint","IMPRINT",EDGE,{"derivedFrom":subQ5}),1.0]])]});}
            var Q45;
            {var subQ0=sQuery(id+"F0.wireOp",EDGE,"E314.MirrorCS");Q45=makeQuery(id+"F0.imprint","IMPRINT",FACE,{"disambiguationData":[TD([[makeQuery(id+"F0.imprint","IMPRINT",EDGE,{"derivedFrom":subQ0}),1.0]])]});}
            var Q46;
            Q46=makeQuery(id+"F0.imprint","IMPRINT",FACE,{"disambiguationData":[TD([[makeQuery(id+"F0.imprint","IMPRINT",EDGE,{"derivedFrom":sQuery(id+"F0.wireOp",EDGE,"E325.MirrorCS")}),1.0]])]});
            var Q47;
            {var subQ5=sQuery(id+"F0.wireOp",EDGE,"E315.MirrorCS");Q47=makeQuery(id+"F0.imprint","IMPRINT",FACE,{"disambiguationData":[TD([[makeQuery(id+"F0.imprint","IMPRINT",EDGE,{"derivedFrom":subQ5}),1.0]])]});}
            extrude(context, id + "F1", {"entities" : qUnion([Q0, Q1, Q2, Q3, Q4, Q5, Q6, Q7, Q8, Q9, Q10, Q11, Q12, Q13, Q14, Q15, Q16, Q17, Q18, Q19, Q20, Q21, Q22, Q23, Q24, Q25, Q26, Q27, Q28, Q29, Q30, Q31, Q32, Q33, Q34, Q35, Q36, Q37, Q38, Q39, Q40, Q41, Q42, Q43, Q44, Q45, Q46, Q47]), "depth" : 25.4 * mm, "offsetDistance" : 25.4 * mm});
        }
    });
